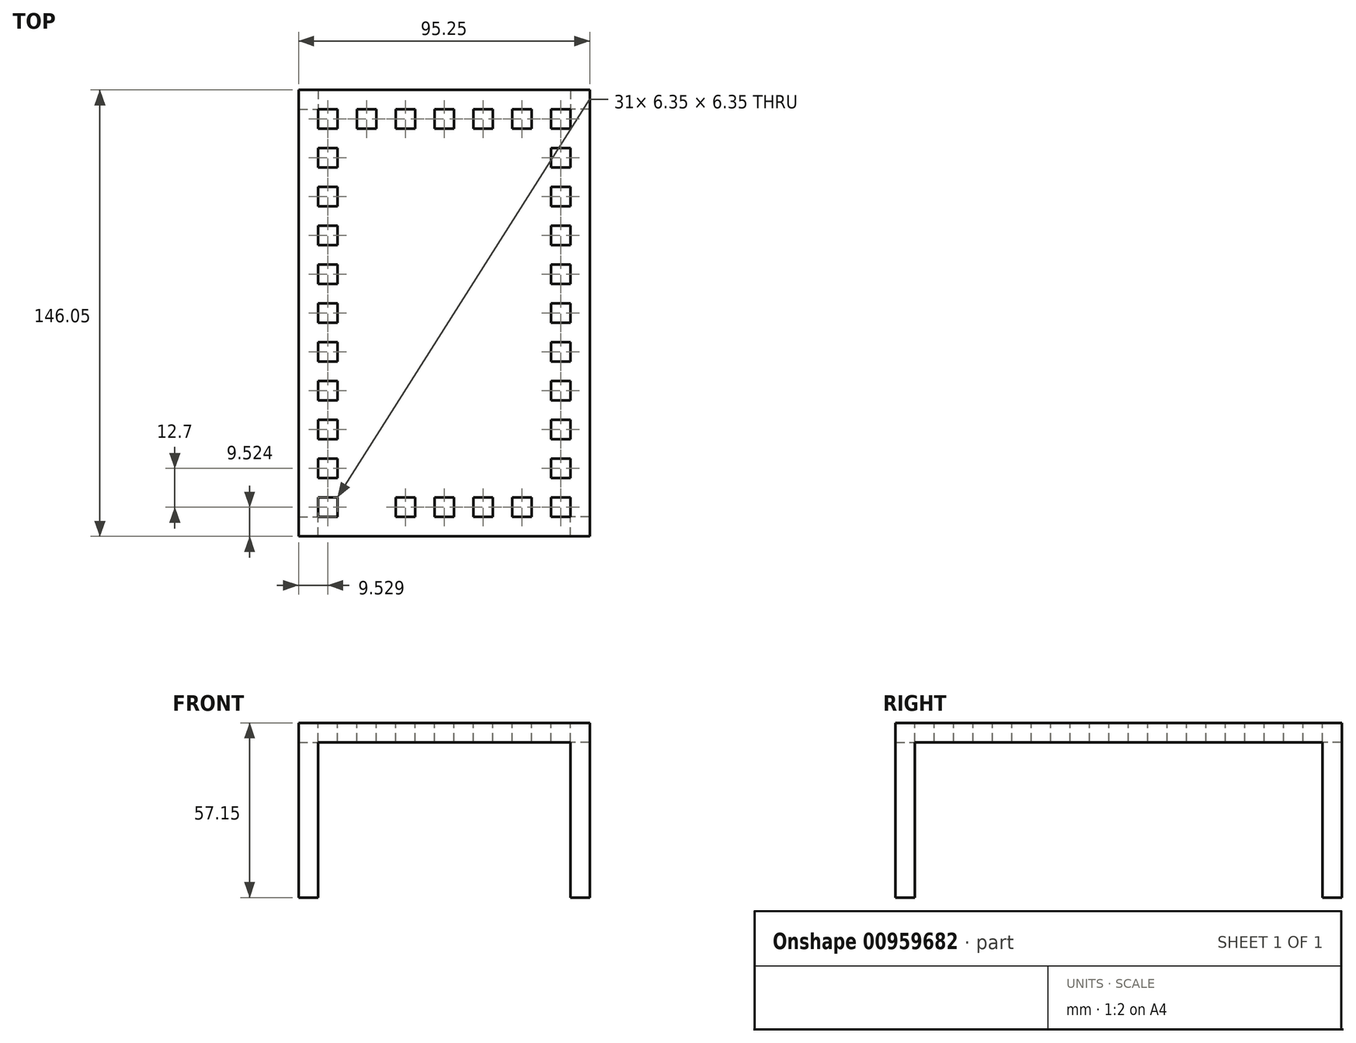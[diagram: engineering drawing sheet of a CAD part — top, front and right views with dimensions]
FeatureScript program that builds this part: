
annotation { "Feature Type Name" : "Feature", "Feature Type Description" : "" }
export const myFeature = defineFeature(function(context is Context, id is Id, definition is map)
    precondition{}
    {
        {
            var Q0;
            Q0=qCreatedBy(makeId("Top.planeOp"),FACE);
            var sketch = newSketch(context, id + "F0", { "sketchPlane" : qUnion([Q0])});
            skLineSegment(sketch, "E0.bottom", {"start": v(-168.58, 47.54) * mm, "end": v(-73.33, 47.54) * mm});
            skLineSegment(sketch, "E0.top", {"start": v(-168.58, -98.51) * mm, "end": v(-73.33, -98.51) * mm});
            skLineSegment(sketch, "E0.left", {"start": v(-168.58, 47.54) * mm, "end": v(-168.58, -98.51) * mm});
            skLineSegment(sketch, "E0.right", {"start": v(-73.33, 47.54) * mm, "end": v(-73.33, -98.51) * mm});
            skSolve(sketch);
        }
        {
            var Q0;
            Q0=makeQuery(id+"F0.imprint","IMPRINT",FACE,{"disambiguationData":[TD([[makeQuery(id+"F0.imprint","IMPRINT",EDGE,{"derivedFrom":sQuery(id+"F0.wireOp",EDGE,"E0.bottom")}),-1.0]])]});
            extrude(context, id + "F1", {"entities" : qUnion([Q0]), "depth" : 6.35 * mm, "offsetDistance" : 25.4 * mm});
        }
        {
            var Q0;
            Q0=makeQuery(id+"F1.opExtrude","CAP_FACE",FACE,{"disambiguationData":[OSD([sQuery(id+"F0.wireOp",EDGE,"E0.bottom"),sQuery(id+"F0.wireOp",EDGE,"E0.top"),sQuery(id+"F0.wireOp",EDGE,"E0.left"),sQuery(id+"F0.wireOp",EDGE,"E0.right")])],"isStart":false});
            var sketch = newSketch(context, id + "F2", { "sketchPlane" : qUnion([Q0])});
            skLineSegment(sketch, "E1.bottom", {"start": v(-162.23, 41.19) * mm, "end": v(-155.88, 41.19) * mm});
            skLineSegment(sketch, "E1.top", {"start": v(-162.23, 34.84) * mm, "end": v(-155.88, 34.84) * mm});
            skLineSegment(sketch, "E1.left", {"start": v(-162.23, 41.19) * mm, "end": v(-162.23, 34.84) * mm});
            skLineSegment(sketch, "E1.right", {"start": v(-155.88, 41.19) * mm, "end": v(-155.88, 34.84) * mm});
            skLineSegment(sketch, "E2.1.0.3", {"start": v(-149.53, 41.19) * mm, "end": v(-149.53, 34.84) * mm});
            skLineSegment(sketch, "E2.2.0.0", {"start": v(-149.53, 41.19) * mm, "end": v(-143.18, 41.19) * mm});
            skLineSegment(sketch, "E2.2.0.1", {"start": v(-149.53, 41.19) * mm, "end": v(-149.53, 34.84) * mm});
            skLineSegment(sketch, "E2.2.0.2", {"start": v(-149.53, 34.84) * mm, "end": v(-143.18, 34.84) * mm});
            skLineSegment(sketch, "E2.2.0.3", {"start": v(-143.18, 41.19) * mm, "end": v(-143.18, 34.84) * mm});
            skLineSegment(sketch, "E2.3.0.1", {"start": v(-143.18, 41.19) * mm, "end": v(-143.18, 34.84) * mm});
            skLineSegment(sketch, "E2.3.0.3", {"start": v(-136.83, 41.19) * mm, "end": v(-136.83, 34.84) * mm});
            skLineSegment(sketch, "E2.4.0.0", {"start": v(-136.83, 41.19) * mm, "end": v(-130.48, 41.19) * mm});
            skLineSegment(sketch, "E2.4.0.1", {"start": v(-136.83, 41.19) * mm, "end": v(-136.83, 34.84) * mm});
            skLineSegment(sketch, "E2.4.0.2", {"start": v(-136.83, 34.84) * mm, "end": v(-130.48, 34.84) * mm});
            skLineSegment(sketch, "E2.4.0.3", {"start": v(-130.48, 41.19) * mm, "end": v(-130.48, 34.84) * mm});
            skLineSegment(sketch, "E2.5.0.1", {"start": v(-130.48, 41.19) * mm, "end": v(-130.48, 34.84) * mm});
            skLineSegment(sketch, "E2.5.0.3", {"start": v(-124.13, 41.19) * mm, "end": v(-124.13, 34.84) * mm});
            skLineSegment(sketch, "E2.6.0.0", {"start": v(-124.13, 41.19) * mm, "end": v(-117.78, 41.19) * mm});
            skLineSegment(sketch, "E2.6.0.1", {"start": v(-124.13, 41.19) * mm, "end": v(-124.13, 34.84) * mm});
            skLineSegment(sketch, "E2.6.0.2", {"start": v(-124.13, 34.84) * mm, "end": v(-117.78, 34.84) * mm});
            skLineSegment(sketch, "E2.6.0.3", {"start": v(-117.78, 41.19) * mm, "end": v(-117.78, 34.84) * mm});
            skLineSegment(sketch, "E2.7.0.1", {"start": v(-117.78, 41.19) * mm, "end": v(-117.78, 34.84) * mm});
            skLineSegment(sketch, "E2.7.0.3", {"start": v(-111.43, 41.19) * mm, "end": v(-111.43, 34.84) * mm});
            skLineSegment(sketch, "E2.8.0.0", {"start": v(-111.43, 41.19) * mm, "end": v(-105.08, 41.19) * mm});
            skLineSegment(sketch, "E2.8.0.1", {"start": v(-111.43, 41.19) * mm, "end": v(-111.43, 34.84) * mm});
            skLineSegment(sketch, "E2.8.0.2", {"start": v(-111.43, 34.84) * mm, "end": v(-105.08, 34.84) * mm});
            skLineSegment(sketch, "E2.8.0.3", {"start": v(-105.08, 41.19) * mm, "end": v(-105.08, 34.84) * mm});
            skLineSegment(sketch, "E2.9.0.1", {"start": v(-105.08, 41.19) * mm, "end": v(-105.08, 34.84) * mm});
            skLineSegment(sketch, "E2.9.0.3", {"start": v(-98.73, 41.19) * mm, "end": v(-98.73, 34.84) * mm});
            skLineSegment(sketch, "E2.10.0.0", {"start": v(-98.73, 41.19) * mm, "end": v(-92.38, 41.19) * mm});
            skLineSegment(sketch, "E2.10.0.1", {"start": v(-98.73, 41.19) * mm, "end": v(-98.73, 34.84) * mm});
            skLineSegment(sketch, "E2.10.0.2", {"start": v(-98.73, 34.84) * mm, "end": v(-92.38, 34.84) * mm});
            skLineSegment(sketch, "E2.10.0.3", {"start": v(-92.38, 41.19) * mm, "end": v(-92.38, 34.84) * mm});
            skLineSegment(sketch, "E2.11.0.1", {"start": v(-92.38, 41.19) * mm, "end": v(-92.38, 34.84) * mm});
            skLineSegment(sketch, "E2.11.0.3", {"start": v(-86.03, 41.19) * mm, "end": v(-86.03, 34.84) * mm});
            skLineSegment(sketch, "E2.12.0.0", {"start": v(-86.03, 41.19) * mm, "end": v(-79.68, 41.19) * mm});
            skLineSegment(sketch, "E2.12.0.1", {"start": v(-86.03, 41.19) * mm, "end": v(-86.03, 34.84) * mm});
            skLineSegment(sketch, "E2.12.0.2", {"start": v(-86.03, 34.84) * mm, "end": v(-79.68, 34.84) * mm});
            skLineSegment(sketch, "E2.12.0.3", {"start": v(-79.68, 41.19) * mm, "end": v(-79.68, 34.84) * mm});
            skLineSegment(sketch, "E2.direction1", {"start": v(-162.23, 41.19) * mm, "end": v(-155.88, 41.19) * mm, "construction": true});
            skLineSegment(sketch, "E3.1.0.3", {"start": v(-124.13, 28.49) * mm, "end": v(-117.78, 28.49) * mm});
            skLineSegment(sketch, "E3.1.0.4", {"start": v(-149.53, 28.49) * mm, "end": v(-143.18, 28.49) * mm});
            skLineSegment(sketch, "E3.1.0.5", {"start": v(-98.73, 28.49) * mm, "end": v(-92.38, 28.49) * mm});
            skLineSegment(sketch, "E3.1.0.17", {"start": v(-162.23, 28.49) * mm, "end": v(-155.88, 28.49) * mm});
            skLineSegment(sketch, "E3.1.0.30", {"start": v(-86.03, 28.49) * mm, "end": v(-79.68, 28.49) * mm});
            skLineSegment(sketch, "E3.1.0.31", {"start": v(-111.43, 28.49) * mm, "end": v(-105.08, 28.49) * mm});
            skLineSegment(sketch, "E3.1.0.32", {"start": v(-136.83, 28.49) * mm, "end": v(-130.48, 28.49) * mm});
            skLineSegment(sketch, "E3.2.0.0", {"start": v(-149.53, 28.49) * mm, "end": v(-143.18, 28.49) * mm});
            skLineSegment(sketch, "E3.2.0.1", {"start": v(-149.53, 28.49) * mm, "end": v(-149.53, 22.14) * mm});
            skLineSegment(sketch, "E3.2.0.3", {"start": v(-124.13, 22.14) * mm, "end": v(-117.78, 22.14) * mm});
            skLineSegment(sketch, "E3.2.0.4", {"start": v(-149.53, 22.14) * mm, "end": v(-143.18, 22.14) * mm});
            skLineSegment(sketch, "E3.2.0.5", {"start": v(-98.73, 22.14) * mm, "end": v(-92.38, 22.14) * mm});
            skLineSegment(sketch, "E3.2.0.7", {"start": v(-98.73, 28.49) * mm, "end": v(-92.38, 28.49) * mm});
            skLineSegment(sketch, "E3.2.0.8", {"start": v(-124.13, 28.49) * mm, "end": v(-117.78, 28.49) * mm});
            skLineSegment(sketch, "E3.2.0.11", {"start": v(-143.18, 28.49) * mm, "end": v(-143.18, 22.14) * mm});
            skLineSegment(sketch, "E3.2.0.12", {"start": v(-98.73, 28.49) * mm, "end": v(-98.73, 22.14) * mm});
            skLineSegment(sketch, "E3.2.0.13", {"start": v(-124.13, 28.49) * mm, "end": v(-124.13, 22.14) * mm});
            skLineSegment(sketch, "E3.2.0.17", {"start": v(-162.23, 22.14) * mm, "end": v(-155.88, 22.14) * mm});
            skLineSegment(sketch, "E3.2.0.20", {"start": v(-162.23, 28.49) * mm, "end": v(-162.23, 22.14) * mm});
            skLineSegment(sketch, "E3.2.0.21", {"start": v(-162.23, 28.49) * mm, "end": v(-155.88, 28.49) * mm, "construction": true});
            skLineSegment(sketch, "E3.2.0.22", {"start": v(-92.38, 28.49) * mm, "end": v(-92.38, 22.14) * mm});
            skLineSegment(sketch, "E3.2.0.24", {"start": v(-117.78, 28.49) * mm, "end": v(-117.78, 22.14) * mm});
            skLineSegment(sketch, "E3.2.0.26", {"start": v(-79.68, 28.49) * mm, "end": v(-79.68, 22.14) * mm});
            skLineSegment(sketch, "E3.2.0.27", {"start": v(-105.08, 28.49) * mm, "end": v(-105.08, 22.14) * mm});
            skLineSegment(sketch, "E3.2.0.28", {"start": v(-130.48, 28.49) * mm, "end": v(-130.48, 22.14) * mm});
            skLineSegment(sketch, "E3.2.0.30", {"start": v(-86.03, 22.14) * mm, "end": v(-79.68, 22.14) * mm});
            skLineSegment(sketch, "E3.2.0.31", {"start": v(-111.43, 22.14) * mm, "end": v(-105.08, 22.14) * mm});
            skLineSegment(sketch, "E3.2.0.32", {"start": v(-136.83, 22.14) * mm, "end": v(-130.48, 22.14) * mm});
            skLineSegment(sketch, "E3.2.0.33", {"start": v(-155.88, 28.49) * mm, "end": v(-155.88, 22.14) * mm});
            skLineSegment(sketch, "E3.2.0.34", {"start": v(-86.03, 28.49) * mm, "end": v(-86.03, 22.14) * mm});
            skLineSegment(sketch, "E3.2.0.35", {"start": v(-111.43, 28.49) * mm, "end": v(-111.43, 22.14) * mm});
            skLineSegment(sketch, "E3.2.0.36", {"start": v(-136.83, 28.49) * mm, "end": v(-136.83, 22.14) * mm});
            skLineSegment(sketch, "E3.2.0.37", {"start": v(-86.03, 28.49) * mm, "end": v(-79.68, 28.49) * mm});
            skLineSegment(sketch, "E3.2.0.38", {"start": v(-111.43, 28.49) * mm, "end": v(-105.08, 28.49) * mm});
            skLineSegment(sketch, "E3.2.0.39", {"start": v(-136.83, 28.49) * mm, "end": v(-130.48, 28.49) * mm});
            skLineSegment(sketch, "E3.2.0.40", {"start": v(-98.73, 28.49) * mm, "end": v(-98.73, 22.14) * mm});
            skLineSegment(sketch, "E3.2.0.41", {"start": v(-117.78, 28.49) * mm, "end": v(-117.78, 22.14) * mm});
            skLineSegment(sketch, "E3.2.0.42", {"start": v(-136.83, 28.49) * mm, "end": v(-136.83, 22.14) * mm});
            skLineSegment(sketch, "E3.2.0.43", {"start": v(-143.18, 28.49) * mm, "end": v(-143.18, 22.14) * mm});
            skLineSegment(sketch, "E3.2.0.44", {"start": v(-124.13, 28.49) * mm, "end": v(-124.13, 22.14) * mm});
            skLineSegment(sketch, "E3.2.0.45", {"start": v(-149.53, 28.49) * mm, "end": v(-149.53, 22.14) * mm});
            skLineSegment(sketch, "E3.2.0.46", {"start": v(-92.38, 28.49) * mm, "end": v(-92.38, 22.14) * mm});
            skLineSegment(sketch, "E3.2.0.47", {"start": v(-162.23, 28.49) * mm, "end": v(-155.88, 28.49) * mm});
            skLineSegment(sketch, "E3.2.0.48", {"start": v(-105.08, 28.49) * mm, "end": v(-105.08, 22.14) * mm});
            skLineSegment(sketch, "E3.2.0.49", {"start": v(-130.48, 28.49) * mm, "end": v(-130.48, 22.14) * mm});
            skLineSegment(sketch, "E3.2.0.50", {"start": v(-155.88, 28.49) * mm, "end": v(-155.88, 22.14) * mm});
            skLineSegment(sketch, "E3.2.0.51", {"start": v(-86.03, 28.49) * mm, "end": v(-86.03, 22.14) * mm});
            skLineSegment(sketch, "E3.2.0.52", {"start": v(-111.43, 28.49) * mm, "end": v(-111.43, 22.14) * mm});
            skLineSegment(sketch, "E3.3.0.0", {"start": v(-149.53, 22.14) * mm, "end": v(-143.18, 22.14) * mm});
            skLineSegment(sketch, "E3.3.0.3", {"start": v(-124.13, 15.79) * mm, "end": v(-117.78, 15.79) * mm});
            skLineSegment(sketch, "E3.3.0.4", {"start": v(-149.53, 15.79) * mm, "end": v(-143.18, 15.79) * mm});
            skLineSegment(sketch, "E3.3.0.5", {"start": v(-98.73, 15.79) * mm, "end": v(-92.38, 15.79) * mm});
            skLineSegment(sketch, "E3.3.0.7", {"start": v(-98.73, 22.14) * mm, "end": v(-92.38, 22.14) * mm});
            skLineSegment(sketch, "E3.3.0.8", {"start": v(-124.13, 22.14) * mm, "end": v(-117.78, 22.14) * mm});
            skLineSegment(sketch, "E3.3.0.17", {"start": v(-162.23, 15.79) * mm, "end": v(-155.88, 15.79) * mm});
            skLineSegment(sketch, "E3.3.0.21", {"start": v(-162.23, 22.14) * mm, "end": v(-155.88, 22.14) * mm, "construction": true});
            skLineSegment(sketch, "E3.3.0.30", {"start": v(-86.03, 15.79) * mm, "end": v(-79.68, 15.79) * mm});
            skLineSegment(sketch, "E3.3.0.31", {"start": v(-111.43, 15.79) * mm, "end": v(-105.08, 15.79) * mm});
            skLineSegment(sketch, "E3.3.0.32", {"start": v(-136.83, 15.79) * mm, "end": v(-130.48, 15.79) * mm});
            skLineSegment(sketch, "E3.3.0.37", {"start": v(-86.03, 22.14) * mm, "end": v(-79.68, 22.14) * mm});
            skLineSegment(sketch, "E3.3.0.38", {"start": v(-111.43, 22.14) * mm, "end": v(-105.08, 22.14) * mm});
            skLineSegment(sketch, "E3.3.0.39", {"start": v(-136.83, 22.14) * mm, "end": v(-130.48, 22.14) * mm});
            skLineSegment(sketch, "E3.3.0.47", {"start": v(-162.23, 22.14) * mm, "end": v(-155.88, 22.14) * mm});
            skLineSegment(sketch, "E3.4.0.0", {"start": v(-149.53, 15.79) * mm, "end": v(-143.18, 15.79) * mm});
            skLineSegment(sketch, "E3.4.0.1", {"start": v(-149.53, 15.79) * mm, "end": v(-149.53, 9.44) * mm});
            skLineSegment(sketch, "E3.4.0.3", {"start": v(-124.13, 9.44) * mm, "end": v(-117.78, 9.44) * mm});
            skLineSegment(sketch, "E3.4.0.4", {"start": v(-149.53, 9.44) * mm, "end": v(-143.18, 9.44) * mm});
            skLineSegment(sketch, "E3.4.0.5", {"start": v(-98.73, 9.44) * mm, "end": v(-92.38, 9.44) * mm});
            skLineSegment(sketch, "E3.4.0.7", {"start": v(-98.73, 15.79) * mm, "end": v(-92.38, 15.79) * mm});
            skLineSegment(sketch, "E3.4.0.8", {"start": v(-124.13, 15.79) * mm, "end": v(-117.78, 15.79) * mm});
            skLineSegment(sketch, "E3.4.0.11", {"start": v(-143.18, 15.79) * mm, "end": v(-143.18, 9.44) * mm});
            skLineSegment(sketch, "E3.4.0.12", {"start": v(-98.73, 15.79) * mm, "end": v(-98.73, 9.44) * mm});
            skLineSegment(sketch, "E3.4.0.13", {"start": v(-124.13, 15.79) * mm, "end": v(-124.13, 9.44) * mm});
            skLineSegment(sketch, "E3.4.0.17", {"start": v(-162.23, 9.44) * mm, "end": v(-155.88, 9.44) * mm});
            skLineSegment(sketch, "E3.4.0.20", {"start": v(-162.23, 15.79) * mm, "end": v(-162.23, 9.44) * mm});
            skLineSegment(sketch, "E3.4.0.21", {"start": v(-162.23, 15.79) * mm, "end": v(-155.88, 15.79) * mm, "construction": true});
            skLineSegment(sketch, "E3.4.0.22", {"start": v(-92.38, 15.79) * mm, "end": v(-92.38, 9.44) * mm});
            skLineSegment(sketch, "E3.4.0.24", {"start": v(-117.78, 15.79) * mm, "end": v(-117.78, 9.44) * mm});
            skLineSegment(sketch, "E3.4.0.26", {"start": v(-79.68, 15.79) * mm, "end": v(-79.68, 9.44) * mm});
            skLineSegment(sketch, "E3.4.0.27", {"start": v(-105.08, 15.79) * mm, "end": v(-105.08, 9.44) * mm});
            skLineSegment(sketch, "E3.4.0.28", {"start": v(-130.48, 15.79) * mm, "end": v(-130.48, 9.44) * mm});
            skLineSegment(sketch, "E3.4.0.30", {"start": v(-86.03, 9.44) * mm, "end": v(-79.68, 9.44) * mm});
            skLineSegment(sketch, "E3.4.0.31", {"start": v(-111.43, 9.44) * mm, "end": v(-105.08, 9.44) * mm});
            skLineSegment(sketch, "E3.4.0.32", {"start": v(-136.83, 9.44) * mm, "end": v(-130.48, 9.44) * mm});
            skLineSegment(sketch, "E3.4.0.33", {"start": v(-155.88, 15.79) * mm, "end": v(-155.88, 9.44) * mm});
            skLineSegment(sketch, "E3.4.0.34", {"start": v(-86.03, 15.79) * mm, "end": v(-86.03, 9.44) * mm});
            skLineSegment(sketch, "E3.4.0.35", {"start": v(-111.43, 15.79) * mm, "end": v(-111.43, 9.44) * mm});
            skLineSegment(sketch, "E3.4.0.36", {"start": v(-136.83, 15.79) * mm, "end": v(-136.83, 9.44) * mm});
            skLineSegment(sketch, "E3.4.0.37", {"start": v(-86.03, 15.79) * mm, "end": v(-79.68, 15.79) * mm});
            skLineSegment(sketch, "E3.4.0.38", {"start": v(-111.43, 15.79) * mm, "end": v(-105.08, 15.79) * mm});
            skLineSegment(sketch, "E3.4.0.39", {"start": v(-136.83, 15.79) * mm, "end": v(-130.48, 15.79) * mm});
            skLineSegment(sketch, "E3.4.0.40", {"start": v(-98.73, 15.79) * mm, "end": v(-98.73, 9.44) * mm});
            skLineSegment(sketch, "E3.4.0.41", {"start": v(-117.78, 15.79) * mm, "end": v(-117.78, 9.44) * mm});
            skLineSegment(sketch, "E3.4.0.42", {"start": v(-136.83, 15.79) * mm, "end": v(-136.83, 9.44) * mm});
            skLineSegment(sketch, "E3.4.0.43", {"start": v(-143.18, 15.79) * mm, "end": v(-143.18, 9.44) * mm});
            skLineSegment(sketch, "E3.4.0.44", {"start": v(-124.13, 15.79) * mm, "end": v(-124.13, 9.44) * mm});
            skLineSegment(sketch, "E3.4.0.45", {"start": v(-149.53, 15.79) * mm, "end": v(-149.53, 9.44) * mm});
            skLineSegment(sketch, "E3.4.0.46", {"start": v(-92.38, 15.79) * mm, "end": v(-92.38, 9.44) * mm});
            skLineSegment(sketch, "E3.4.0.47", {"start": v(-162.23, 15.79) * mm, "end": v(-155.88, 15.79) * mm});
            skLineSegment(sketch, "E3.4.0.48", {"start": v(-105.08, 15.79) * mm, "end": v(-105.08, 9.44) * mm});
            skLineSegment(sketch, "E3.4.0.49", {"start": v(-130.48, 15.79) * mm, "end": v(-130.48, 9.44) * mm});
            skLineSegment(sketch, "E3.4.0.50", {"start": v(-155.88, 15.79) * mm, "end": v(-155.88, 9.44) * mm});
            skLineSegment(sketch, "E3.4.0.51", {"start": v(-86.03, 15.79) * mm, "end": v(-86.03, 9.44) * mm});
            skLineSegment(sketch, "E3.4.0.52", {"start": v(-111.43, 15.79) * mm, "end": v(-111.43, 9.44) * mm});
            skLineSegment(sketch, "E3.5.0.0", {"start": v(-149.53, 9.44) * mm, "end": v(-143.18, 9.44) * mm});
            skLineSegment(sketch, "E3.5.0.3", {"start": v(-124.13, 3.09) * mm, "end": v(-117.78, 3.09) * mm});
            skLineSegment(sketch, "E3.5.0.4", {"start": v(-149.53, 3.09) * mm, "end": v(-143.18, 3.09) * mm});
            skLineSegment(sketch, "E3.5.0.5", {"start": v(-98.73, 3.09) * mm, "end": v(-92.38, 3.09) * mm});
            skLineSegment(sketch, "E3.5.0.7", {"start": v(-98.73, 9.44) * mm, "end": v(-92.38, 9.44) * mm});
            skLineSegment(sketch, "E3.5.0.8", {"start": v(-124.13, 9.44) * mm, "end": v(-117.78, 9.44) * mm});
            skLineSegment(sketch, "E3.5.0.17", {"start": v(-162.23, 3.09) * mm, "end": v(-155.88, 3.09) * mm});
            skLineSegment(sketch, "E3.5.0.21", {"start": v(-162.23, 9.44) * mm, "end": v(-155.88, 9.44) * mm, "construction": true});
            skLineSegment(sketch, "E3.5.0.30", {"start": v(-86.03, 3.09) * mm, "end": v(-79.68, 3.09) * mm});
            skLineSegment(sketch, "E3.5.0.31", {"start": v(-111.43, 3.09) * mm, "end": v(-105.08, 3.09) * mm});
            skLineSegment(sketch, "E3.5.0.32", {"start": v(-136.83, 3.09) * mm, "end": v(-130.48, 3.09) * mm});
            skLineSegment(sketch, "E3.5.0.37", {"start": v(-86.03, 9.44) * mm, "end": v(-79.68, 9.44) * mm});
            skLineSegment(sketch, "E3.5.0.38", {"start": v(-111.43, 9.44) * mm, "end": v(-105.08, 9.44) * mm});
            skLineSegment(sketch, "E3.5.0.39", {"start": v(-136.83, 9.44) * mm, "end": v(-130.48, 9.44) * mm});
            skLineSegment(sketch, "E3.5.0.47", {"start": v(-162.23, 9.44) * mm, "end": v(-155.88, 9.44) * mm});
            skLineSegment(sketch, "E3.6.0.0", {"start": v(-149.53, 3.09) * mm, "end": v(-143.18, 3.09) * mm});
            skLineSegment(sketch, "E3.6.0.1", {"start": v(-149.53, 3.09) * mm, "end": v(-149.53, -3.26) * mm});
            skLineSegment(sketch, "E3.6.0.3", {"start": v(-124.13, -3.26) * mm, "end": v(-117.78, -3.26) * mm});
            skLineSegment(sketch, "E3.6.0.4", {"start": v(-149.53, -3.26) * mm, "end": v(-143.18, -3.26) * mm});
            skLineSegment(sketch, "E3.6.0.5", {"start": v(-98.73, -3.26) * mm, "end": v(-92.38, -3.26) * mm});
            skLineSegment(sketch, "E3.6.0.7", {"start": v(-98.73, 3.09) * mm, "end": v(-92.38, 3.09) * mm});
            skLineSegment(sketch, "E3.6.0.8", {"start": v(-124.13, 3.09) * mm, "end": v(-117.78, 3.09) * mm});
            skLineSegment(sketch, "E3.6.0.11", {"start": v(-143.18, 3.09) * mm, "end": v(-143.18, -3.26) * mm});
            skLineSegment(sketch, "E3.6.0.12", {"start": v(-98.73, 3.09) * mm, "end": v(-98.73, -3.26) * mm});
            skLineSegment(sketch, "E3.6.0.13", {"start": v(-124.13, 3.09) * mm, "end": v(-124.13, -3.26) * mm});
            skLineSegment(sketch, "E3.6.0.17", {"start": v(-162.23, -3.26) * mm, "end": v(-155.88, -3.26) * mm});
            skLineSegment(sketch, "E3.6.0.20", {"start": v(-162.23, 3.09) * mm, "end": v(-162.23, -3.26) * mm});
            skLineSegment(sketch, "E3.6.0.21", {"start": v(-162.23, 3.09) * mm, "end": v(-155.88, 3.09) * mm, "construction": true});
            skLineSegment(sketch, "E3.6.0.22", {"start": v(-92.38, 3.09) * mm, "end": v(-92.38, -3.26) * mm});
            skLineSegment(sketch, "E3.6.0.24", {"start": v(-117.78, 3.09) * mm, "end": v(-117.78, -3.26) * mm});
            skLineSegment(sketch, "E3.6.0.26", {"start": v(-79.68, 3.09) * mm, "end": v(-79.68, -3.26) * mm});
            skLineSegment(sketch, "E3.6.0.27", {"start": v(-105.08, 3.09) * mm, "end": v(-105.08, -3.26) * mm});
            skLineSegment(sketch, "E3.6.0.28", {"start": v(-130.48, 3.09) * mm, "end": v(-130.48, -3.26) * mm});
            skLineSegment(sketch, "E3.6.0.30", {"start": v(-86.03, -3.26) * mm, "end": v(-79.68, -3.26) * mm});
            skLineSegment(sketch, "E3.6.0.31", {"start": v(-111.43, -3.26) * mm, "end": v(-105.08, -3.26) * mm});
            skLineSegment(sketch, "E3.6.0.32", {"start": v(-136.83, -3.26) * mm, "end": v(-130.48, -3.26) * mm});
            skLineSegment(sketch, "E3.6.0.33", {"start": v(-155.88, 3.09) * mm, "end": v(-155.88, -3.26) * mm});
            skLineSegment(sketch, "E3.6.0.34", {"start": v(-86.03, 3.09) * mm, "end": v(-86.03, -3.26) * mm});
            skLineSegment(sketch, "E3.6.0.35", {"start": v(-111.43, 3.09) * mm, "end": v(-111.43, -3.26) * mm});
            skLineSegment(sketch, "E3.6.0.36", {"start": v(-136.83, 3.09) * mm, "end": v(-136.83, -3.26) * mm});
            skLineSegment(sketch, "E3.6.0.37", {"start": v(-86.03, 3.09) * mm, "end": v(-79.68, 3.09) * mm});
            skLineSegment(sketch, "E3.6.0.38", {"start": v(-111.43, 3.09) * mm, "end": v(-105.08, 3.09) * mm});
            skLineSegment(sketch, "E3.6.0.39", {"start": v(-136.83, 3.09) * mm, "end": v(-130.48, 3.09) * mm});
            skLineSegment(sketch, "E3.6.0.40", {"start": v(-98.73, 3.09) * mm, "end": v(-98.73, -3.26) * mm});
            skLineSegment(sketch, "E3.6.0.41", {"start": v(-117.78, 3.09) * mm, "end": v(-117.78, -3.26) * mm});
            skLineSegment(sketch, "E3.6.0.42", {"start": v(-136.83, 3.09) * mm, "end": v(-136.83, -3.26) * mm});
            skLineSegment(sketch, "E3.6.0.43", {"start": v(-143.18, 3.09) * mm, "end": v(-143.18, -3.26) * mm});
            skLineSegment(sketch, "E3.6.0.44", {"start": v(-124.13, 3.09) * mm, "end": v(-124.13, -3.26) * mm});
            skLineSegment(sketch, "E3.6.0.45", {"start": v(-149.53, 3.09) * mm, "end": v(-149.53, -3.26) * mm});
            skLineSegment(sketch, "E3.6.0.46", {"start": v(-92.38, 3.09) * mm, "end": v(-92.38, -3.26) * mm});
            skLineSegment(sketch, "E3.6.0.47", {"start": v(-162.23, 3.09) * mm, "end": v(-155.88, 3.09) * mm});
            skLineSegment(sketch, "E3.6.0.48", {"start": v(-105.08, 3.09) * mm, "end": v(-105.08, -3.26) * mm});
            skLineSegment(sketch, "E3.6.0.49", {"start": v(-130.48, 3.09) * mm, "end": v(-130.48, -3.26) * mm});
            skLineSegment(sketch, "E3.6.0.50", {"start": v(-155.88, 3.09) * mm, "end": v(-155.88, -3.26) * mm});
            skLineSegment(sketch, "E3.6.0.51", {"start": v(-86.03, 3.09) * mm, "end": v(-86.03, -3.26) * mm});
            skLineSegment(sketch, "E3.6.0.52", {"start": v(-111.43, 3.09) * mm, "end": v(-111.43, -3.26) * mm});
            skLineSegment(sketch, "E3.7.0.0", {"start": v(-149.53, -3.26) * mm, "end": v(-143.18, -3.26) * mm});
            skLineSegment(sketch, "E3.7.0.3", {"start": v(-124.13, -9.61) * mm, "end": v(-117.78, -9.61) * mm});
            skLineSegment(sketch, "E3.7.0.4", {"start": v(-149.53, -9.61) * mm, "end": v(-143.18, -9.61) * mm});
            skLineSegment(sketch, "E3.7.0.5", {"start": v(-98.73, -9.61) * mm, "end": v(-92.38, -9.61) * mm});
            skLineSegment(sketch, "E3.7.0.7", {"start": v(-98.73, -3.26) * mm, "end": v(-92.38, -3.26) * mm});
            skLineSegment(sketch, "E3.7.0.8", {"start": v(-124.13, -3.26) * mm, "end": v(-117.78, -3.26) * mm});
            skLineSegment(sketch, "E3.7.0.17", {"start": v(-162.23, -9.61) * mm, "end": v(-155.88, -9.61) * mm});
            skLineSegment(sketch, "E3.7.0.21", {"start": v(-162.23, -3.26) * mm, "end": v(-155.88, -3.26) * mm, "construction": true});
            skLineSegment(sketch, "E3.7.0.30", {"start": v(-86.03, -9.61) * mm, "end": v(-79.68, -9.61) * mm});
            skLineSegment(sketch, "E3.7.0.31", {"start": v(-111.43, -9.61) * mm, "end": v(-105.08, -9.61) * mm});
            skLineSegment(sketch, "E3.7.0.32", {"start": v(-136.83, -9.61) * mm, "end": v(-130.48, -9.61) * mm});
            skLineSegment(sketch, "E3.7.0.37", {"start": v(-86.03, -3.26) * mm, "end": v(-79.68, -3.26) * mm});
            skLineSegment(sketch, "E3.7.0.38", {"start": v(-111.43, -3.26) * mm, "end": v(-105.08, -3.26) * mm});
            skLineSegment(sketch, "E3.7.0.39", {"start": v(-136.83, -3.26) * mm, "end": v(-130.48, -3.26) * mm});
            skLineSegment(sketch, "E3.7.0.47", {"start": v(-162.23, -3.26) * mm, "end": v(-155.88, -3.26) * mm});
            skLineSegment(sketch, "E3.8.0.0", {"start": v(-149.53, -9.61) * mm, "end": v(-143.18, -9.61) * mm});
            skLineSegment(sketch, "E3.8.0.1", {"start": v(-149.53, -9.61) * mm, "end": v(-149.53, -15.96) * mm});
            skLineSegment(sketch, "E3.8.0.3", {"start": v(-124.13, -15.96) * mm, "end": v(-117.78, -15.96) * mm});
            skLineSegment(sketch, "E3.8.0.4", {"start": v(-149.53, -15.96) * mm, "end": v(-143.18, -15.96) * mm});
            skLineSegment(sketch, "E3.8.0.5", {"start": v(-98.73, -15.96) * mm, "end": v(-92.38, -15.96) * mm});
            skLineSegment(sketch, "E3.8.0.7", {"start": v(-98.73, -9.61) * mm, "end": v(-92.38, -9.61) * mm});
            skLineSegment(sketch, "E3.8.0.8", {"start": v(-124.13, -9.61) * mm, "end": v(-117.78, -9.61) * mm});
            skLineSegment(sketch, "E3.8.0.11", {"start": v(-143.18, -9.61) * mm, "end": v(-143.18, -15.96) * mm});
            skLineSegment(sketch, "E3.8.0.12", {"start": v(-98.73, -9.61) * mm, "end": v(-98.73, -15.96) * mm});
            skLineSegment(sketch, "E3.8.0.13", {"start": v(-124.13, -9.61) * mm, "end": v(-124.13, -15.96) * mm});
            skLineSegment(sketch, "E3.8.0.17", {"start": v(-162.23, -15.96) * mm, "end": v(-155.88, -15.96) * mm});
            skLineSegment(sketch, "E3.8.0.20", {"start": v(-162.23, -9.61) * mm, "end": v(-162.23, -15.96) * mm});
            skLineSegment(sketch, "E3.8.0.21", {"start": v(-162.23, -9.61) * mm, "end": v(-155.88, -9.61) * mm, "construction": true});
            skLineSegment(sketch, "E3.8.0.22", {"start": v(-92.38, -9.61) * mm, "end": v(-92.38, -15.96) * mm});
            skLineSegment(sketch, "E3.8.0.24", {"start": v(-117.78, -9.61) * mm, "end": v(-117.78, -15.96) * mm});
            skLineSegment(sketch, "E3.8.0.26", {"start": v(-79.68, -9.61) * mm, "end": v(-79.68, -15.96) * mm});
            skLineSegment(sketch, "E3.8.0.27", {"start": v(-105.08, -9.61) * mm, "end": v(-105.08, -15.96) * mm});
            skLineSegment(sketch, "E3.8.0.28", {"start": v(-130.48, -9.61) * mm, "end": v(-130.48, -15.96) * mm});
            skLineSegment(sketch, "E3.8.0.30", {"start": v(-86.03, -15.96) * mm, "end": v(-79.68, -15.96) * mm});
            skLineSegment(sketch, "E3.8.0.31", {"start": v(-111.43, -15.96) * mm, "end": v(-105.08, -15.96) * mm});
            skLineSegment(sketch, "E3.8.0.32", {"start": v(-136.83, -15.96) * mm, "end": v(-130.48, -15.96) * mm});
            skLineSegment(sketch, "E3.8.0.33", {"start": v(-155.88, -9.61) * mm, "end": v(-155.88, -15.96) * mm});
            skLineSegment(sketch, "E3.8.0.34", {"start": v(-86.03, -9.61) * mm, "end": v(-86.03, -15.96) * mm});
            skLineSegment(sketch, "E3.8.0.35", {"start": v(-111.43, -9.61) * mm, "end": v(-111.43, -15.96) * mm});
            skLineSegment(sketch, "E3.8.0.36", {"start": v(-136.83, -9.61) * mm, "end": v(-136.83, -15.96) * mm});
            skLineSegment(sketch, "E3.8.0.37", {"start": v(-86.03, -9.61) * mm, "end": v(-79.68, -9.61) * mm});
            skLineSegment(sketch, "E3.8.0.38", {"start": v(-111.43, -9.61) * mm, "end": v(-105.08, -9.61) * mm});
            skLineSegment(sketch, "E3.8.0.39", {"start": v(-136.83, -9.61) * mm, "end": v(-130.48, -9.61) * mm});
            skLineSegment(sketch, "E3.8.0.40", {"start": v(-98.73, -9.61) * mm, "end": v(-98.73, -15.96) * mm});
            skLineSegment(sketch, "E3.8.0.41", {"start": v(-117.78, -9.61) * mm, "end": v(-117.78, -15.96) * mm});
            skLineSegment(sketch, "E3.8.0.42", {"start": v(-136.83, -9.61) * mm, "end": v(-136.83, -15.96) * mm});
            skLineSegment(sketch, "E3.8.0.43", {"start": v(-143.18, -9.61) * mm, "end": v(-143.18, -15.96) * mm});
            skLineSegment(sketch, "E3.8.0.44", {"start": v(-124.13, -9.61) * mm, "end": v(-124.13, -15.96) * mm});
            skLineSegment(sketch, "E3.8.0.45", {"start": v(-149.53, -9.61) * mm, "end": v(-149.53, -15.96) * mm});
            skLineSegment(sketch, "E3.8.0.46", {"start": v(-92.38, -9.61) * mm, "end": v(-92.38, -15.96) * mm});
            skLineSegment(sketch, "E3.8.0.47", {"start": v(-162.23, -9.61) * mm, "end": v(-155.88, -9.61) * mm});
            skLineSegment(sketch, "E3.8.0.48", {"start": v(-105.08, -9.61) * mm, "end": v(-105.08, -15.96) * mm});
            skLineSegment(sketch, "E3.8.0.49", {"start": v(-130.48, -9.61) * mm, "end": v(-130.48, -15.96) * mm});
            skLineSegment(sketch, "E3.8.0.50", {"start": v(-155.88, -9.61) * mm, "end": v(-155.88, -15.96) * mm});
            skLineSegment(sketch, "E3.8.0.51", {"start": v(-86.03, -9.61) * mm, "end": v(-86.03, -15.96) * mm});
            skLineSegment(sketch, "E3.8.0.52", {"start": v(-111.43, -9.61) * mm, "end": v(-111.43, -15.96) * mm});
            skLineSegment(sketch, "E3.9.0.0", {"start": v(-149.53, -15.96) * mm, "end": v(-143.18, -15.96) * mm});
            skLineSegment(sketch, "E3.9.0.3", {"start": v(-124.13, -22.31) * mm, "end": v(-117.78, -22.31) * mm});
            skLineSegment(sketch, "E3.9.0.4", {"start": v(-149.53, -22.31) * mm, "end": v(-143.18, -22.31) * mm});
            skLineSegment(sketch, "E3.9.0.5", {"start": v(-98.73, -22.31) * mm, "end": v(-92.38, -22.31) * mm});
            skLineSegment(sketch, "E3.9.0.7", {"start": v(-98.73, -15.96) * mm, "end": v(-92.38, -15.96) * mm});
            skLineSegment(sketch, "E3.9.0.8", {"start": v(-124.13, -15.96) * mm, "end": v(-117.78, -15.96) * mm});
            skLineSegment(sketch, "E3.9.0.17", {"start": v(-162.23, -22.31) * mm, "end": v(-155.88, -22.31) * mm});
            skLineSegment(sketch, "E3.9.0.21", {"start": v(-162.23, -15.96) * mm, "end": v(-155.88, -15.96) * mm, "construction": true});
            skLineSegment(sketch, "E3.9.0.30", {"start": v(-86.03, -22.31) * mm, "end": v(-79.68, -22.31) * mm});
            skLineSegment(sketch, "E3.9.0.31", {"start": v(-111.43, -22.31) * mm, "end": v(-105.08, -22.31) * mm});
            skLineSegment(sketch, "E3.9.0.32", {"start": v(-136.83, -22.31) * mm, "end": v(-130.48, -22.31) * mm});
            skLineSegment(sketch, "E3.9.0.37", {"start": v(-86.03, -15.96) * mm, "end": v(-79.68, -15.96) * mm});
            skLineSegment(sketch, "E3.9.0.38", {"start": v(-111.43, -15.96) * mm, "end": v(-105.08, -15.96) * mm});
            skLineSegment(sketch, "E3.9.0.39", {"start": v(-136.83, -15.96) * mm, "end": v(-130.48, -15.96) * mm});
            skLineSegment(sketch, "E3.9.0.47", {"start": v(-162.23, -15.96) * mm, "end": v(-155.88, -15.96) * mm});
            skLineSegment(sketch, "E3.10.0.0", {"start": v(-149.53, -22.31) * mm, "end": v(-143.18, -22.31) * mm});
            skLineSegment(sketch, "E3.10.0.1", {"start": v(-149.53, -22.31) * mm, "end": v(-149.53, -28.66) * mm});
            skLineSegment(sketch, "E3.10.0.3", {"start": v(-124.13, -28.66) * mm, "end": v(-117.78, -28.66) * mm});
            skLineSegment(sketch, "E3.10.0.4", {"start": v(-149.53, -28.66) * mm, "end": v(-143.18, -28.66) * mm});
            skLineSegment(sketch, "E3.10.0.5", {"start": v(-98.73, -28.66) * mm, "end": v(-92.38, -28.66) * mm});
            skLineSegment(sketch, "E3.10.0.7", {"start": v(-98.73, -22.31) * mm, "end": v(-92.38, -22.31) * mm});
            skLineSegment(sketch, "E3.10.0.8", {"start": v(-124.13, -22.31) * mm, "end": v(-117.78, -22.31) * mm});
            skLineSegment(sketch, "E3.10.0.11", {"start": v(-143.18, -22.31) * mm, "end": v(-143.18, -28.66) * mm});
            skLineSegment(sketch, "E3.10.0.12", {"start": v(-98.73, -22.31) * mm, "end": v(-98.73, -28.66) * mm});
            skLineSegment(sketch, "E3.10.0.13", {"start": v(-124.13, -22.31) * mm, "end": v(-124.13, -28.66) * mm});
            skLineSegment(sketch, "E3.10.0.17", {"start": v(-162.23, -28.66) * mm, "end": v(-155.88, -28.66) * mm});
            skLineSegment(sketch, "E3.10.0.20", {"start": v(-162.23, -22.31) * mm, "end": v(-162.23, -28.66) * mm});
            skLineSegment(sketch, "E3.10.0.21", {"start": v(-162.23, -22.31) * mm, "end": v(-155.88, -22.31) * mm, "construction": true});
            skLineSegment(sketch, "E3.10.0.22", {"start": v(-92.38, -22.31) * mm, "end": v(-92.38, -28.66) * mm});
            skLineSegment(sketch, "E3.10.0.24", {"start": v(-117.78, -22.31) * mm, "end": v(-117.78, -28.66) * mm});
            skLineSegment(sketch, "E3.10.0.26", {"start": v(-79.68, -22.31) * mm, "end": v(-79.68, -28.66) * mm});
            skLineSegment(sketch, "E3.10.0.27", {"start": v(-105.08, -22.31) * mm, "end": v(-105.08, -28.66) * mm});
            skLineSegment(sketch, "E3.10.0.28", {"start": v(-130.48, -22.31) * mm, "end": v(-130.48, -28.66) * mm});
            skLineSegment(sketch, "E3.10.0.30", {"start": v(-86.03, -28.66) * mm, "end": v(-79.68, -28.66) * mm});
            skLineSegment(sketch, "E3.10.0.31", {"start": v(-111.43, -28.66) * mm, "end": v(-105.08, -28.66) * mm});
            skLineSegment(sketch, "E3.10.0.32", {"start": v(-136.83, -28.66) * mm, "end": v(-130.48, -28.66) * mm});
            skLineSegment(sketch, "E3.10.0.33", {"start": v(-155.88, -22.31) * mm, "end": v(-155.88, -28.66) * mm});
            skLineSegment(sketch, "E3.10.0.34", {"start": v(-86.03, -22.31) * mm, "end": v(-86.03, -28.66) * mm});
            skLineSegment(sketch, "E3.10.0.35", {"start": v(-111.43, -22.31) * mm, "end": v(-111.43, -28.66) * mm});
            skLineSegment(sketch, "E3.10.0.36", {"start": v(-136.83, -22.31) * mm, "end": v(-136.83, -28.66) * mm});
            skLineSegment(sketch, "E3.10.0.37", {"start": v(-86.03, -22.31) * mm, "end": v(-79.68, -22.31) * mm});
            skLineSegment(sketch, "E3.10.0.38", {"start": v(-111.43, -22.31) * mm, "end": v(-105.08, -22.31) * mm});
            skLineSegment(sketch, "E3.10.0.39", {"start": v(-136.83, -22.31) * mm, "end": v(-130.48, -22.31) * mm});
            skLineSegment(sketch, "E3.10.0.40", {"start": v(-98.73, -22.31) * mm, "end": v(-98.73, -28.66) * mm});
            skLineSegment(sketch, "E3.10.0.41", {"start": v(-117.78, -22.31) * mm, "end": v(-117.78, -28.66) * mm});
            skLineSegment(sketch, "E3.10.0.42", {"start": v(-136.83, -22.31) * mm, "end": v(-136.83, -28.66) * mm});
            skLineSegment(sketch, "E3.10.0.43", {"start": v(-143.18, -22.31) * mm, "end": v(-143.18, -28.66) * mm});
            skLineSegment(sketch, "E3.10.0.44", {"start": v(-124.13, -22.31) * mm, "end": v(-124.13, -28.66) * mm});
            skLineSegment(sketch, "E3.10.0.45", {"start": v(-149.53, -22.31) * mm, "end": v(-149.53, -28.66) * mm});
            skLineSegment(sketch, "E3.10.0.46", {"start": v(-92.38, -22.31) * mm, "end": v(-92.38, -28.66) * mm});
            skLineSegment(sketch, "E3.10.0.47", {"start": v(-162.23, -22.31) * mm, "end": v(-155.88, -22.31) * mm});
            skLineSegment(sketch, "E3.10.0.48", {"start": v(-105.08, -22.31) * mm, "end": v(-105.08, -28.66) * mm});
            skLineSegment(sketch, "E3.10.0.49", {"start": v(-130.48, -22.31) * mm, "end": v(-130.48, -28.66) * mm});
            skLineSegment(sketch, "E3.10.0.50", {"start": v(-155.88, -22.31) * mm, "end": v(-155.88, -28.66) * mm});
            skLineSegment(sketch, "E3.10.0.51", {"start": v(-86.03, -22.31) * mm, "end": v(-86.03, -28.66) * mm});
            skLineSegment(sketch, "E3.10.0.52", {"start": v(-111.43, -22.31) * mm, "end": v(-111.43, -28.66) * mm});
            skLineSegment(sketch, "E3.11.0.0", {"start": v(-149.53, -28.66) * mm, "end": v(-143.18, -28.66) * mm});
            skLineSegment(sketch, "E3.11.0.3", {"start": v(-124.13, -35.01) * mm, "end": v(-117.78, -35.01) * mm});
            skLineSegment(sketch, "E3.11.0.4", {"start": v(-149.53, -35.01) * mm, "end": v(-143.18, -35.01) * mm});
            skLineSegment(sketch, "E3.11.0.5", {"start": v(-98.73, -35.01) * mm, "end": v(-92.38, -35.01) * mm});
            skLineSegment(sketch, "E3.11.0.7", {"start": v(-98.73, -28.66) * mm, "end": v(-92.38, -28.66) * mm});
            skLineSegment(sketch, "E3.11.0.8", {"start": v(-124.13, -28.66) * mm, "end": v(-117.78, -28.66) * mm});
            skLineSegment(sketch, "E3.11.0.17", {"start": v(-162.23, -35.01) * mm, "end": v(-155.88, -35.01) * mm});
            skLineSegment(sketch, "E3.11.0.21", {"start": v(-162.23, -28.66) * mm, "end": v(-155.88, -28.66) * mm, "construction": true});
            skLineSegment(sketch, "E3.11.0.30", {"start": v(-86.03, -35.01) * mm, "end": v(-79.68, -35.01) * mm});
            skLineSegment(sketch, "E3.11.0.31", {"start": v(-111.43, -35.01) * mm, "end": v(-105.08, -35.01) * mm});
            skLineSegment(sketch, "E3.11.0.32", {"start": v(-136.83, -35.01) * mm, "end": v(-130.48, -35.01) * mm});
            skLineSegment(sketch, "E3.11.0.37", {"start": v(-86.03, -28.66) * mm, "end": v(-79.68, -28.66) * mm});
            skLineSegment(sketch, "E3.11.0.38", {"start": v(-111.43, -28.66) * mm, "end": v(-105.08, -28.66) * mm});
            skLineSegment(sketch, "E3.11.0.39", {"start": v(-136.83, -28.66) * mm, "end": v(-130.48, -28.66) * mm});
            skLineSegment(sketch, "E3.11.0.47", {"start": v(-162.23, -28.66) * mm, "end": v(-155.88, -28.66) * mm});
            skLineSegment(sketch, "E3.12.0.0", {"start": v(-149.53, -35.01) * mm, "end": v(-143.18, -35.01) * mm});
            skLineSegment(sketch, "E3.12.0.1", {"start": v(-149.53, -35.01) * mm, "end": v(-149.53, -41.36) * mm});
            skLineSegment(sketch, "E3.12.0.3", {"start": v(-124.13, -41.36) * mm, "end": v(-117.78, -41.36) * mm});
            skLineSegment(sketch, "E3.12.0.4", {"start": v(-149.53, -41.36) * mm, "end": v(-143.18, -41.36) * mm});
            skLineSegment(sketch, "E3.12.0.5", {"start": v(-98.73, -41.36) * mm, "end": v(-92.38, -41.36) * mm});
            skLineSegment(sketch, "E3.12.0.7", {"start": v(-98.73, -35.01) * mm, "end": v(-92.38, -35.01) * mm});
            skLineSegment(sketch, "E3.12.0.8", {"start": v(-124.13, -35.01) * mm, "end": v(-117.78, -35.01) * mm});
            skLineSegment(sketch, "E3.12.0.11", {"start": v(-143.18, -35.01) * mm, "end": v(-143.18, -41.36) * mm});
            skLineSegment(sketch, "E3.12.0.12", {"start": v(-98.73, -35.01) * mm, "end": v(-98.73, -41.36) * mm});
            skLineSegment(sketch, "E3.12.0.13", {"start": v(-124.13, -35.01) * mm, "end": v(-124.13, -41.36) * mm});
            skLineSegment(sketch, "E3.12.0.17", {"start": v(-162.23, -41.36) * mm, "end": v(-155.88, -41.36) * mm});
            skLineSegment(sketch, "E3.12.0.20", {"start": v(-162.23, -35.01) * mm, "end": v(-162.23, -41.36) * mm});
            skLineSegment(sketch, "E3.12.0.21", {"start": v(-162.23, -35.01) * mm, "end": v(-155.88, -35.01) * mm, "construction": true});
            skLineSegment(sketch, "E3.12.0.22", {"start": v(-92.38, -35.01) * mm, "end": v(-92.38, -41.36) * mm});
            skLineSegment(sketch, "E3.12.0.24", {"start": v(-117.78, -35.01) * mm, "end": v(-117.78, -41.36) * mm});
            skLineSegment(sketch, "E3.12.0.26", {"start": v(-79.68, -35.01) * mm, "end": v(-79.68, -41.36) * mm});
            skLineSegment(sketch, "E3.12.0.27", {"start": v(-105.08, -35.01) * mm, "end": v(-105.08, -41.36) * mm});
            skLineSegment(sketch, "E3.12.0.28", {"start": v(-130.48, -35.01) * mm, "end": v(-130.48, -41.36) * mm});
            skLineSegment(sketch, "E3.12.0.30", {"start": v(-86.03, -41.36) * mm, "end": v(-79.68, -41.36) * mm});
            skLineSegment(sketch, "E3.12.0.31", {"start": v(-111.43, -41.36) * mm, "end": v(-105.08, -41.36) * mm});
            skLineSegment(sketch, "E3.12.0.32", {"start": v(-136.83, -41.36) * mm, "end": v(-130.48, -41.36) * mm});
            skLineSegment(sketch, "E3.12.0.33", {"start": v(-155.88, -35.01) * mm, "end": v(-155.88, -41.36) * mm});
            skLineSegment(sketch, "E3.12.0.34", {"start": v(-86.03, -35.01) * mm, "end": v(-86.03, -41.36) * mm});
            skLineSegment(sketch, "E3.12.0.35", {"start": v(-111.43, -35.01) * mm, "end": v(-111.43, -41.36) * mm});
            skLineSegment(sketch, "E3.12.0.36", {"start": v(-136.83, -35.01) * mm, "end": v(-136.83, -41.36) * mm});
            skLineSegment(sketch, "E3.12.0.37", {"start": v(-86.03, -35.01) * mm, "end": v(-79.68, -35.01) * mm});
            skLineSegment(sketch, "E3.12.0.38", {"start": v(-111.43, -35.01) * mm, "end": v(-105.08, -35.01) * mm});
            skLineSegment(sketch, "E3.12.0.39", {"start": v(-136.83, -35.01) * mm, "end": v(-130.48, -35.01) * mm});
            skLineSegment(sketch, "E3.12.0.40", {"start": v(-98.73, -35.01) * mm, "end": v(-98.73, -41.36) * mm});
            skLineSegment(sketch, "E3.12.0.41", {"start": v(-117.78, -35.01) * mm, "end": v(-117.78, -41.36) * mm});
            skLineSegment(sketch, "E3.12.0.42", {"start": v(-136.83, -35.01) * mm, "end": v(-136.83, -41.36) * mm});
            skLineSegment(sketch, "E3.12.0.43", {"start": v(-143.18, -35.01) * mm, "end": v(-143.18, -41.36) * mm});
            skLineSegment(sketch, "E3.12.0.44", {"start": v(-124.13, -35.01) * mm, "end": v(-124.13, -41.36) * mm});
            skLineSegment(sketch, "E3.12.0.45", {"start": v(-149.53, -35.01) * mm, "end": v(-149.53, -41.36) * mm});
            skLineSegment(sketch, "E3.12.0.46", {"start": v(-92.38, -35.01) * mm, "end": v(-92.38, -41.36) * mm});
            skLineSegment(sketch, "E3.12.0.47", {"start": v(-162.23, -35.01) * mm, "end": v(-155.88, -35.01) * mm});
            skLineSegment(sketch, "E3.12.0.48", {"start": v(-105.08, -35.01) * mm, "end": v(-105.08, -41.36) * mm});
            skLineSegment(sketch, "E3.12.0.49", {"start": v(-130.48, -35.01) * mm, "end": v(-130.48, -41.36) * mm});
            skLineSegment(sketch, "E3.12.0.50", {"start": v(-155.88, -35.01) * mm, "end": v(-155.88, -41.36) * mm});
            skLineSegment(sketch, "E3.12.0.51", {"start": v(-86.03, -35.01) * mm, "end": v(-86.03, -41.36) * mm});
            skLineSegment(sketch, "E3.12.0.52", {"start": v(-111.43, -35.01) * mm, "end": v(-111.43, -41.36) * mm});
            skLineSegment(sketch, "E3.13.0.0", {"start": v(-149.53, -41.36) * mm, "end": v(-143.18, -41.36) * mm});
            skLineSegment(sketch, "E3.13.0.3", {"start": v(-124.13, -47.71) * mm, "end": v(-117.78, -47.71) * mm});
            skLineSegment(sketch, "E3.13.0.4", {"start": v(-149.53, -47.71) * mm, "end": v(-143.18, -47.71) * mm});
            skLineSegment(sketch, "E3.13.0.5", {"start": v(-98.73, -47.71) * mm, "end": v(-92.38, -47.71) * mm});
            skLineSegment(sketch, "E3.13.0.7", {"start": v(-98.73, -41.36) * mm, "end": v(-92.38, -41.36) * mm});
            skLineSegment(sketch, "E3.13.0.8", {"start": v(-124.13, -41.36) * mm, "end": v(-117.78, -41.36) * mm});
            skLineSegment(sketch, "E3.13.0.17", {"start": v(-162.23, -47.71) * mm, "end": v(-155.88, -47.71) * mm});
            skLineSegment(sketch, "E3.13.0.21", {"start": v(-162.23, -41.36) * mm, "end": v(-155.88, -41.36) * mm, "construction": true});
            skLineSegment(sketch, "E3.13.0.30", {"start": v(-86.03, -47.71) * mm, "end": v(-79.68, -47.71) * mm});
            skLineSegment(sketch, "E3.13.0.31", {"start": v(-111.43, -47.71) * mm, "end": v(-105.08, -47.71) * mm});
            skLineSegment(sketch, "E3.13.0.32", {"start": v(-136.83, -47.71) * mm, "end": v(-130.48, -47.71) * mm});
            skLineSegment(sketch, "E3.13.0.37", {"start": v(-86.03, -41.36) * mm, "end": v(-79.68, -41.36) * mm});
            skLineSegment(sketch, "E3.13.0.38", {"start": v(-111.43, -41.36) * mm, "end": v(-105.08, -41.36) * mm});
            skLineSegment(sketch, "E3.13.0.39", {"start": v(-136.83, -41.36) * mm, "end": v(-130.48, -41.36) * mm});
            skLineSegment(sketch, "E3.13.0.47", {"start": v(-162.23, -41.36) * mm, "end": v(-155.88, -41.36) * mm});
            skLineSegment(sketch, "E3.14.0.0", {"start": v(-149.53, -47.71) * mm, "end": v(-143.18, -47.71) * mm});
            skLineSegment(sketch, "E3.14.0.1", {"start": v(-149.53, -47.71) * mm, "end": v(-149.53, -54.06) * mm});
            skLineSegment(sketch, "E3.14.0.3", {"start": v(-124.13, -54.06) * mm, "end": v(-117.78, -54.06) * mm});
            skLineSegment(sketch, "E3.14.0.4", {"start": v(-149.53, -54.06) * mm, "end": v(-143.18, -54.06) * mm});
            skLineSegment(sketch, "E3.14.0.5", {"start": v(-98.73, -54.06) * mm, "end": v(-92.38, -54.06) * mm});
            skLineSegment(sketch, "E3.14.0.7", {"start": v(-98.73, -47.71) * mm, "end": v(-92.38, -47.71) * mm});
            skLineSegment(sketch, "E3.14.0.8", {"start": v(-124.13, -47.71) * mm, "end": v(-117.78, -47.71) * mm});
            skLineSegment(sketch, "E3.14.0.11", {"start": v(-143.18, -47.71) * mm, "end": v(-143.18, -54.06) * mm});
            skLineSegment(sketch, "E3.14.0.12", {"start": v(-98.73, -47.71) * mm, "end": v(-98.73, -54.06) * mm});
            skLineSegment(sketch, "E3.14.0.13", {"start": v(-124.13, -47.71) * mm, "end": v(-124.13, -54.06) * mm});
            skLineSegment(sketch, "E3.14.0.17", {"start": v(-162.23, -54.06) * mm, "end": v(-155.88, -54.06) * mm});
            skLineSegment(sketch, "E3.14.0.20", {"start": v(-162.23, -47.71) * mm, "end": v(-162.23, -54.06) * mm});
            skLineSegment(sketch, "E3.14.0.21", {"start": v(-162.23, -47.71) * mm, "end": v(-155.88, -47.71) * mm, "construction": true});
            skLineSegment(sketch, "E3.14.0.22", {"start": v(-92.38, -47.71) * mm, "end": v(-92.38, -54.06) * mm});
            skLineSegment(sketch, "E3.14.0.24", {"start": v(-117.78, -47.71) * mm, "end": v(-117.78, -54.06) * mm});
            skLineSegment(sketch, "E3.14.0.26", {"start": v(-79.68, -47.71) * mm, "end": v(-79.68, -54.06) * mm});
            skLineSegment(sketch, "E3.14.0.27", {"start": v(-105.08, -47.71) * mm, "end": v(-105.08, -54.06) * mm});
            skLineSegment(sketch, "E3.14.0.28", {"start": v(-130.48, -47.71) * mm, "end": v(-130.48, -54.06) * mm});
            skLineSegment(sketch, "E3.14.0.30", {"start": v(-86.03, -54.06) * mm, "end": v(-79.68, -54.06) * mm});
            skLineSegment(sketch, "E3.14.0.31", {"start": v(-111.43, -54.06) * mm, "end": v(-105.08, -54.06) * mm});
            skLineSegment(sketch, "E3.14.0.32", {"start": v(-136.83, -54.06) * mm, "end": v(-130.48, -54.06) * mm});
            skLineSegment(sketch, "E3.14.0.33", {"start": v(-155.88, -47.71) * mm, "end": v(-155.88, -54.06) * mm});
            skLineSegment(sketch, "E3.14.0.34", {"start": v(-86.03, -47.71) * mm, "end": v(-86.03, -54.06) * mm});
            skLineSegment(sketch, "E3.14.0.35", {"start": v(-111.43, -47.71) * mm, "end": v(-111.43, -54.06) * mm});
            skLineSegment(sketch, "E3.14.0.36", {"start": v(-136.83, -47.71) * mm, "end": v(-136.83, -54.06) * mm});
            skLineSegment(sketch, "E3.14.0.37", {"start": v(-86.03, -47.71) * mm, "end": v(-79.68, -47.71) * mm});
            skLineSegment(sketch, "E3.14.0.38", {"start": v(-111.43, -47.71) * mm, "end": v(-105.08, -47.71) * mm});
            skLineSegment(sketch, "E3.14.0.39", {"start": v(-136.83, -47.71) * mm, "end": v(-130.48, -47.71) * mm});
            skLineSegment(sketch, "E3.14.0.40", {"start": v(-98.73, -47.71) * mm, "end": v(-98.73, -54.06) * mm});
            skLineSegment(sketch, "E3.14.0.41", {"start": v(-117.78, -47.71) * mm, "end": v(-117.78, -54.06) * mm});
            skLineSegment(sketch, "E3.14.0.42", {"start": v(-136.83, -47.71) * mm, "end": v(-136.83, -54.06) * mm});
            skLineSegment(sketch, "E3.14.0.43", {"start": v(-143.18, -47.71) * mm, "end": v(-143.18, -54.06) * mm});
            skLineSegment(sketch, "E3.14.0.44", {"start": v(-124.13, -47.71) * mm, "end": v(-124.13, -54.06) * mm});
            skLineSegment(sketch, "E3.14.0.45", {"start": v(-149.53, -47.71) * mm, "end": v(-149.53, -54.06) * mm});
            skLineSegment(sketch, "E3.14.0.46", {"start": v(-92.38, -47.71) * mm, "end": v(-92.38, -54.06) * mm});
            skLineSegment(sketch, "E3.14.0.47", {"start": v(-162.23, -47.71) * mm, "end": v(-155.88, -47.71) * mm});
            skLineSegment(sketch, "E3.14.0.48", {"start": v(-105.08, -47.71) * mm, "end": v(-105.08, -54.06) * mm});
            skLineSegment(sketch, "E3.14.0.49", {"start": v(-130.48, -47.71) * mm, "end": v(-130.48, -54.06) * mm});
            skLineSegment(sketch, "E3.14.0.50", {"start": v(-155.88, -47.71) * mm, "end": v(-155.88, -54.06) * mm});
            skLineSegment(sketch, "E3.14.0.51", {"start": v(-86.03, -47.71) * mm, "end": v(-86.03, -54.06) * mm});
            skLineSegment(sketch, "E3.14.0.52", {"start": v(-111.43, -47.71) * mm, "end": v(-111.43, -54.06) * mm});
            skLineSegment(sketch, "E3.15.0.0", {"start": v(-149.53, -54.06) * mm, "end": v(-143.18, -54.06) * mm});
            skLineSegment(sketch, "E3.15.0.3", {"start": v(-124.13, -60.41) * mm, "end": v(-117.78, -60.41) * mm});
            skLineSegment(sketch, "E3.15.0.4", {"start": v(-149.53, -60.41) * mm, "end": v(-143.18, -60.41) * mm});
            skLineSegment(sketch, "E3.15.0.5", {"start": v(-98.73, -60.41) * mm, "end": v(-92.38, -60.41) * mm});
            skLineSegment(sketch, "E3.15.0.7", {"start": v(-98.73, -54.06) * mm, "end": v(-92.38, -54.06) * mm});
            skLineSegment(sketch, "E3.15.0.8", {"start": v(-124.13, -54.06) * mm, "end": v(-117.78, -54.06) * mm});
            skLineSegment(sketch, "E3.15.0.17", {"start": v(-162.23, -60.41) * mm, "end": v(-155.88, -60.41) * mm});
            skLineSegment(sketch, "E3.15.0.21", {"start": v(-162.23, -54.06) * mm, "end": v(-155.88, -54.06) * mm, "construction": true});
            skLineSegment(sketch, "E3.15.0.30", {"start": v(-86.03, -60.41) * mm, "end": v(-79.68, -60.41) * mm});
            skLineSegment(sketch, "E3.15.0.31", {"start": v(-111.43, -60.41) * mm, "end": v(-105.08, -60.41) * mm});
            skLineSegment(sketch, "E3.15.0.32", {"start": v(-136.83, -60.41) * mm, "end": v(-130.48, -60.41) * mm});
            skLineSegment(sketch, "E3.15.0.37", {"start": v(-86.03, -54.06) * mm, "end": v(-79.68, -54.06) * mm});
            skLineSegment(sketch, "E3.15.0.38", {"start": v(-111.43, -54.06) * mm, "end": v(-105.08, -54.06) * mm});
            skLineSegment(sketch, "E3.15.0.39", {"start": v(-136.83, -54.06) * mm, "end": v(-130.48, -54.06) * mm});
            skLineSegment(sketch, "E3.15.0.47", {"start": v(-162.23, -54.06) * mm, "end": v(-155.88, -54.06) * mm});
            skLineSegment(sketch, "E3.16.0.0", {"start": v(-149.53, -60.41) * mm, "end": v(-143.18, -60.41) * mm});
            skLineSegment(sketch, "E3.16.0.1", {"start": v(-149.53, -60.41) * mm, "end": v(-149.53, -66.76) * mm});
            skLineSegment(sketch, "E3.16.0.3", {"start": v(-124.13, -66.76) * mm, "end": v(-117.78, -66.76) * mm});
            skLineSegment(sketch, "E3.16.0.4", {"start": v(-149.53, -66.76) * mm, "end": v(-143.18, -66.76) * mm});
            skLineSegment(sketch, "E3.16.0.5", {"start": v(-98.73, -66.76) * mm, "end": v(-92.38, -66.76) * mm});
            skLineSegment(sketch, "E3.16.0.7", {"start": v(-98.73, -60.41) * mm, "end": v(-92.38, -60.41) * mm});
            skLineSegment(sketch, "E3.16.0.8", {"start": v(-124.13, -60.41) * mm, "end": v(-117.78, -60.41) * mm});
            skLineSegment(sketch, "E3.16.0.11", {"start": v(-143.18, -60.41) * mm, "end": v(-143.18, -66.76) * mm});
            skLineSegment(sketch, "E3.16.0.12", {"start": v(-98.73, -60.41) * mm, "end": v(-98.73, -66.76) * mm});
            skLineSegment(sketch, "E3.16.0.13", {"start": v(-124.13, -60.41) * mm, "end": v(-124.13, -66.76) * mm});
            skLineSegment(sketch, "E3.16.0.17", {"start": v(-162.23, -66.76) * mm, "end": v(-155.88, -66.76) * mm});
            skLineSegment(sketch, "E3.16.0.20", {"start": v(-162.23, -60.41) * mm, "end": v(-162.23, -66.76) * mm});
            skLineSegment(sketch, "E3.16.0.21", {"start": v(-162.23, -60.41) * mm, "end": v(-155.88, -60.41) * mm, "construction": true});
            skLineSegment(sketch, "E3.16.0.22", {"start": v(-92.38, -60.41) * mm, "end": v(-92.38, -66.76) * mm});
            skLineSegment(sketch, "E3.16.0.24", {"start": v(-117.78, -60.41) * mm, "end": v(-117.78, -66.76) * mm});
            skLineSegment(sketch, "E3.16.0.26", {"start": v(-79.68, -60.41) * mm, "end": v(-79.68, -66.76) * mm});
            skLineSegment(sketch, "E3.16.0.27", {"start": v(-105.08, -60.41) * mm, "end": v(-105.08, -66.76) * mm});
            skLineSegment(sketch, "E3.16.0.28", {"start": v(-130.48, -60.41) * mm, "end": v(-130.48, -66.76) * mm});
            skLineSegment(sketch, "E3.16.0.30", {"start": v(-86.03, -66.76) * mm, "end": v(-79.68, -66.76) * mm});
            skLineSegment(sketch, "E3.16.0.31", {"start": v(-111.43, -66.76) * mm, "end": v(-105.08, -66.76) * mm});
            skLineSegment(sketch, "E3.16.0.32", {"start": v(-136.83, -66.76) * mm, "end": v(-130.48, -66.76) * mm});
            skLineSegment(sketch, "E3.16.0.33", {"start": v(-155.88, -60.41) * mm, "end": v(-155.88, -66.76) * mm});
            skLineSegment(sketch, "E3.16.0.34", {"start": v(-86.03, -60.41) * mm, "end": v(-86.03, -66.76) * mm});
            skLineSegment(sketch, "E3.16.0.35", {"start": v(-111.43, -60.41) * mm, "end": v(-111.43, -66.76) * mm});
            skLineSegment(sketch, "E3.16.0.36", {"start": v(-136.83, -60.41) * mm, "end": v(-136.83, -66.76) * mm});
            skLineSegment(sketch, "E3.16.0.37", {"start": v(-86.03, -60.41) * mm, "end": v(-79.68, -60.41) * mm});
            skLineSegment(sketch, "E3.16.0.38", {"start": v(-111.43, -60.41) * mm, "end": v(-105.08, -60.41) * mm});
            skLineSegment(sketch, "E3.16.0.39", {"start": v(-136.83, -60.41) * mm, "end": v(-130.48, -60.41) * mm});
            skLineSegment(sketch, "E3.16.0.40", {"start": v(-98.73, -60.41) * mm, "end": v(-98.73, -66.76) * mm});
            skLineSegment(sketch, "E3.16.0.41", {"start": v(-117.78, -60.41) * mm, "end": v(-117.78, -66.76) * mm});
            skLineSegment(sketch, "E3.16.0.42", {"start": v(-136.83, -60.41) * mm, "end": v(-136.83, -66.76) * mm});
            skLineSegment(sketch, "E3.16.0.43", {"start": v(-143.18, -60.41) * mm, "end": v(-143.18, -66.76) * mm});
            skLineSegment(sketch, "E3.16.0.44", {"start": v(-124.13, -60.41) * mm, "end": v(-124.13, -66.76) * mm});
            skLineSegment(sketch, "E3.16.0.45", {"start": v(-149.53, -60.41) * mm, "end": v(-149.53, -66.76) * mm});
            skLineSegment(sketch, "E3.16.0.46", {"start": v(-92.38, -60.41) * mm, "end": v(-92.38, -66.76) * mm});
            skLineSegment(sketch, "E3.16.0.47", {"start": v(-162.23, -60.41) * mm, "end": v(-155.88, -60.41) * mm});
            skLineSegment(sketch, "E3.16.0.48", {"start": v(-105.08, -60.41) * mm, "end": v(-105.08, -66.76) * mm});
            skLineSegment(sketch, "E3.16.0.49", {"start": v(-130.48, -60.41) * mm, "end": v(-130.48, -66.76) * mm});
            skLineSegment(sketch, "E3.16.0.50", {"start": v(-155.88, -60.41) * mm, "end": v(-155.88, -66.76) * mm});
            skLineSegment(sketch, "E3.16.0.51", {"start": v(-86.03, -60.41) * mm, "end": v(-86.03, -66.76) * mm});
            skLineSegment(sketch, "E3.16.0.52", {"start": v(-111.43, -60.41) * mm, "end": v(-111.43, -66.76) * mm});
            skLineSegment(sketch, "E3.17.0.0", {"start": v(-149.53, -66.76) * mm, "end": v(-143.18, -66.76) * mm});
            skLineSegment(sketch, "E3.17.0.3", {"start": v(-124.13, -73.11) * mm, "end": v(-117.78, -73.11) * mm});
            skLineSegment(sketch, "E3.17.0.4", {"start": v(-149.53, -73.11) * mm, "end": v(-143.18, -73.11) * mm});
            skLineSegment(sketch, "E3.17.0.5", {"start": v(-98.73, -73.11) * mm, "end": v(-92.38, -73.11) * mm});
            skLineSegment(sketch, "E3.17.0.7", {"start": v(-98.73, -66.76) * mm, "end": v(-92.38, -66.76) * mm});
            skLineSegment(sketch, "E3.17.0.8", {"start": v(-124.13, -66.76) * mm, "end": v(-117.78, -66.76) * mm});
            skLineSegment(sketch, "E3.17.0.17", {"start": v(-162.23, -73.11) * mm, "end": v(-155.88, -73.11) * mm});
            skLineSegment(sketch, "E3.17.0.21", {"start": v(-162.23, -66.76) * mm, "end": v(-155.88, -66.76) * mm, "construction": true});
            skLineSegment(sketch, "E3.17.0.30", {"start": v(-86.03, -73.11) * mm, "end": v(-79.68, -73.11) * mm});
            skLineSegment(sketch, "E3.17.0.31", {"start": v(-111.43, -73.11) * mm, "end": v(-105.08, -73.11) * mm});
            skLineSegment(sketch, "E3.17.0.32", {"start": v(-136.83, -73.11) * mm, "end": v(-130.48, -73.11) * mm});
            skLineSegment(sketch, "E3.17.0.37", {"start": v(-86.03, -66.76) * mm, "end": v(-79.68, -66.76) * mm});
            skLineSegment(sketch, "E3.17.0.38", {"start": v(-111.43, -66.76) * mm, "end": v(-105.08, -66.76) * mm});
            skLineSegment(sketch, "E3.17.0.39", {"start": v(-136.83, -66.76) * mm, "end": v(-130.48, -66.76) * mm});
            skLineSegment(sketch, "E3.17.0.47", {"start": v(-162.23, -66.76) * mm, "end": v(-155.88, -66.76) * mm});
            skLineSegment(sketch, "E3.18.0.0", {"start": v(-149.53, -73.11) * mm, "end": v(-143.18, -73.11) * mm});
            skLineSegment(sketch, "E3.18.0.1", {"start": v(-149.53, -73.11) * mm, "end": v(-149.53, -79.46) * mm});
            skLineSegment(sketch, "E3.18.0.3", {"start": v(-124.13, -79.46) * mm, "end": v(-117.78, -79.46) * mm});
            skLineSegment(sketch, "E3.18.0.4", {"start": v(-149.53, -79.46) * mm, "end": v(-143.18, -79.46) * mm});
            skLineSegment(sketch, "E3.18.0.5", {"start": v(-98.73, -79.46) * mm, "end": v(-92.38, -79.46) * mm});
            skLineSegment(sketch, "E3.18.0.7", {"start": v(-98.73, -73.11) * mm, "end": v(-92.38, -73.11) * mm});
            skLineSegment(sketch, "E3.18.0.8", {"start": v(-124.13, -73.11) * mm, "end": v(-117.78, -73.11) * mm});
            skLineSegment(sketch, "E3.18.0.11", {"start": v(-143.18, -73.11) * mm, "end": v(-143.18, -79.46) * mm});
            skLineSegment(sketch, "E3.18.0.12", {"start": v(-98.73, -73.11) * mm, "end": v(-98.73, -79.46) * mm});
            skLineSegment(sketch, "E3.18.0.13", {"start": v(-124.13, -73.11) * mm, "end": v(-124.13, -79.46) * mm});
            skLineSegment(sketch, "E3.18.0.17", {"start": v(-162.23, -79.46) * mm, "end": v(-155.88, -79.46) * mm});
            skLineSegment(sketch, "E3.18.0.20", {"start": v(-162.23, -73.11) * mm, "end": v(-162.23, -79.46) * mm});
            skLineSegment(sketch, "E3.18.0.21", {"start": v(-162.23, -73.11) * mm, "end": v(-155.88, -73.11) * mm, "construction": true});
            skLineSegment(sketch, "E3.18.0.22", {"start": v(-92.38, -73.11) * mm, "end": v(-92.38, -79.46) * mm});
            skLineSegment(sketch, "E3.18.0.24", {"start": v(-117.78, -73.11) * mm, "end": v(-117.78, -79.46) * mm});
            skLineSegment(sketch, "E3.18.0.26", {"start": v(-79.68, -73.11) * mm, "end": v(-79.68, -79.46) * mm});
            skLineSegment(sketch, "E3.18.0.27", {"start": v(-105.08, -73.11) * mm, "end": v(-105.08, -79.46) * mm});
            skLineSegment(sketch, "E3.18.0.28", {"start": v(-130.48, -73.11) * mm, "end": v(-130.48, -79.46) * mm});
            skLineSegment(sketch, "E3.18.0.30", {"start": v(-86.03, -79.46) * mm, "end": v(-79.68, -79.46) * mm});
            skLineSegment(sketch, "E3.18.0.31", {"start": v(-111.43, -79.46) * mm, "end": v(-105.08, -79.46) * mm});
            skLineSegment(sketch, "E3.18.0.32", {"start": v(-136.83, -79.46) * mm, "end": v(-130.48, -79.46) * mm});
            skLineSegment(sketch, "E3.18.0.33", {"start": v(-155.88, -73.11) * mm, "end": v(-155.88, -79.46) * mm});
            skLineSegment(sketch, "E3.18.0.34", {"start": v(-86.03, -73.11) * mm, "end": v(-86.03, -79.46) * mm});
            skLineSegment(sketch, "E3.18.0.35", {"start": v(-111.43, -73.11) * mm, "end": v(-111.43, -79.46) * mm});
            skLineSegment(sketch, "E3.18.0.36", {"start": v(-136.83, -73.11) * mm, "end": v(-136.83, -79.46) * mm});
            skLineSegment(sketch, "E3.18.0.37", {"start": v(-86.03, -73.11) * mm, "end": v(-79.68, -73.11) * mm});
            skLineSegment(sketch, "E3.18.0.38", {"start": v(-111.43, -73.11) * mm, "end": v(-105.08, -73.11) * mm});
            skLineSegment(sketch, "E3.18.0.39", {"start": v(-136.83, -73.11) * mm, "end": v(-130.48, -73.11) * mm});
            skLineSegment(sketch, "E3.18.0.40", {"start": v(-98.73, -73.11) * mm, "end": v(-98.73, -79.46) * mm});
            skLineSegment(sketch, "E3.18.0.41", {"start": v(-117.78, -73.11) * mm, "end": v(-117.78, -79.46) * mm});
            skLineSegment(sketch, "E3.18.0.42", {"start": v(-136.83, -73.11) * mm, "end": v(-136.83, -79.46) * mm});
            skLineSegment(sketch, "E3.18.0.43", {"start": v(-143.18, -73.11) * mm, "end": v(-143.18, -79.46) * mm});
            skLineSegment(sketch, "E3.18.0.44", {"start": v(-124.13, -73.11) * mm, "end": v(-124.13, -79.46) * mm});
            skLineSegment(sketch, "E3.18.0.45", {"start": v(-149.53, -73.11) * mm, "end": v(-149.53, -79.46) * mm});
            skLineSegment(sketch, "E3.18.0.46", {"start": v(-92.38, -73.11) * mm, "end": v(-92.38, -79.46) * mm});
            skLineSegment(sketch, "E3.18.0.47", {"start": v(-162.23, -73.11) * mm, "end": v(-155.88, -73.11) * mm});
            skLineSegment(sketch, "E3.18.0.48", {"start": v(-105.08, -73.11) * mm, "end": v(-105.08, -79.46) * mm});
            skLineSegment(sketch, "E3.18.0.49", {"start": v(-130.48, -73.11) * mm, "end": v(-130.48, -79.46) * mm});
            skLineSegment(sketch, "E3.18.0.50", {"start": v(-155.88, -73.11) * mm, "end": v(-155.88, -79.46) * mm});
            skLineSegment(sketch, "E3.18.0.51", {"start": v(-86.03, -73.11) * mm, "end": v(-86.03, -79.46) * mm});
            skLineSegment(sketch, "E3.18.0.52", {"start": v(-111.43, -73.11) * mm, "end": v(-111.43, -79.46) * mm});
            skLineSegment(sketch, "E3.19.0.0", {"start": v(-149.53, -79.46) * mm, "end": v(-143.18, -79.46) * mm});
            skLineSegment(sketch, "E3.19.0.3", {"start": v(-124.13, -85.81) * mm, "end": v(-117.78, -85.81) * mm});
            skLineSegment(sketch, "E3.19.0.4", {"start": v(-149.53, -85.81) * mm, "end": v(-143.18, -85.81) * mm});
            skLineSegment(sketch, "E3.19.0.5", {"start": v(-98.73, -85.81) * mm, "end": v(-92.38, -85.81) * mm});
            skLineSegment(sketch, "E3.19.0.7", {"start": v(-98.73, -79.46) * mm, "end": v(-92.38, -79.46) * mm});
            skLineSegment(sketch, "E3.19.0.8", {"start": v(-124.13, -79.46) * mm, "end": v(-117.78, -79.46) * mm});
            skLineSegment(sketch, "E3.19.0.17", {"start": v(-162.23, -85.81) * mm, "end": v(-155.88, -85.81) * mm});
            skLineSegment(sketch, "E3.19.0.21", {"start": v(-162.23, -79.46) * mm, "end": v(-155.88, -79.46) * mm, "construction": true});
            skLineSegment(sketch, "E3.19.0.30", {"start": v(-86.03, -85.81) * mm, "end": v(-79.68, -85.81) * mm});
            skLineSegment(sketch, "E3.19.0.31", {"start": v(-111.43, -85.81) * mm, "end": v(-105.08, -85.81) * mm});
            skLineSegment(sketch, "E3.19.0.32", {"start": v(-136.83, -85.81) * mm, "end": v(-130.48, -85.81) * mm});
            skLineSegment(sketch, "E3.19.0.37", {"start": v(-86.03, -79.46) * mm, "end": v(-79.68, -79.46) * mm});
            skLineSegment(sketch, "E3.19.0.38", {"start": v(-111.43, -79.46) * mm, "end": v(-105.08, -79.46) * mm});
            skLineSegment(sketch, "E3.19.0.39", {"start": v(-136.83, -79.46) * mm, "end": v(-130.48, -79.46) * mm});
            skLineSegment(sketch, "E3.19.0.47", {"start": v(-162.23, -79.46) * mm, "end": v(-155.88, -79.46) * mm});
            skLineSegment(sketch, "E3.20.0.0", {"start": v(-149.53, -85.81) * mm, "end": v(-143.18, -85.81) * mm});
            skLineSegment(sketch, "E3.20.0.1", {"start": v(-149.53, -85.81) * mm, "end": v(-149.53, -92.16) * mm});
            skLineSegment(sketch, "E3.20.0.3", {"start": v(-124.13, -92.16) * mm, "end": v(-117.78, -92.16) * mm});
            skLineSegment(sketch, "E3.20.0.4", {"start": v(-149.53, -92.16) * mm, "end": v(-143.18, -92.16) * mm});
            skLineSegment(sketch, "E3.20.0.5", {"start": v(-98.73, -92.16) * mm, "end": v(-92.38, -92.16) * mm});
            skLineSegment(sketch, "E3.20.0.7", {"start": v(-98.73, -85.81) * mm, "end": v(-92.38, -85.81) * mm});
            skLineSegment(sketch, "E3.20.0.8", {"start": v(-124.13, -85.81) * mm, "end": v(-117.78, -85.81) * mm});
            skLineSegment(sketch, "E3.20.0.11", {"start": v(-143.18, -85.81) * mm, "end": v(-143.18, -92.16) * mm});
            skLineSegment(sketch, "E3.20.0.12", {"start": v(-98.73, -85.81) * mm, "end": v(-98.73, -92.16) * mm});
            skLineSegment(sketch, "E3.20.0.13", {"start": v(-124.13, -85.81) * mm, "end": v(-124.13, -92.16) * mm});
            skLineSegment(sketch, "E3.20.0.17", {"start": v(-162.23, -92.16) * mm, "end": v(-155.88, -92.16) * mm});
            skLineSegment(sketch, "E3.20.0.20", {"start": v(-162.23, -85.81) * mm, "end": v(-162.23, -92.16) * mm});
            skLineSegment(sketch, "E3.20.0.21", {"start": v(-162.23, -85.81) * mm, "end": v(-155.88, -85.81) * mm, "construction": true});
            skLineSegment(sketch, "E3.20.0.22", {"start": v(-92.38, -85.81) * mm, "end": v(-92.38, -92.16) * mm});
            skLineSegment(sketch, "E3.20.0.24", {"start": v(-117.78, -85.81) * mm, "end": v(-117.78, -92.16) * mm});
            skLineSegment(sketch, "E3.20.0.26", {"start": v(-79.68, -85.81) * mm, "end": v(-79.68, -92.16) * mm});
            skLineSegment(sketch, "E3.20.0.27", {"start": v(-105.08, -85.81) * mm, "end": v(-105.08, -92.16) * mm});
            skLineSegment(sketch, "E3.20.0.28", {"start": v(-130.48, -85.81) * mm, "end": v(-130.48, -92.16) * mm});
            skLineSegment(sketch, "E3.20.0.30", {"start": v(-86.03, -92.16) * mm, "end": v(-79.68, -92.16) * mm});
            skLineSegment(sketch, "E3.20.0.31", {"start": v(-111.43, -92.16) * mm, "end": v(-105.08, -92.16) * mm});
            skLineSegment(sketch, "E3.20.0.32", {"start": v(-136.83, -92.16) * mm, "end": v(-130.48, -92.16) * mm});
            skLineSegment(sketch, "E3.20.0.33", {"start": v(-155.88, -85.81) * mm, "end": v(-155.88, -92.16) * mm});
            skLineSegment(sketch, "E3.20.0.34", {"start": v(-86.03, -85.81) * mm, "end": v(-86.03, -92.16) * mm});
            skLineSegment(sketch, "E3.20.0.35", {"start": v(-111.43, -85.81) * mm, "end": v(-111.43, -92.16) * mm});
            skLineSegment(sketch, "E3.20.0.36", {"start": v(-136.83, -85.81) * mm, "end": v(-136.83, -92.16) * mm});
            skLineSegment(sketch, "E3.20.0.37", {"start": v(-86.03, -85.81) * mm, "end": v(-79.68, -85.81) * mm});
            skLineSegment(sketch, "E3.20.0.38", {"start": v(-111.43, -85.81) * mm, "end": v(-105.08, -85.81) * mm});
            skLineSegment(sketch, "E3.20.0.39", {"start": v(-136.83, -85.81) * mm, "end": v(-130.48, -85.81) * mm});
            skLineSegment(sketch, "E3.20.0.40", {"start": v(-98.73, -85.81) * mm, "end": v(-98.73, -92.16) * mm});
            skLineSegment(sketch, "E3.20.0.41", {"start": v(-117.78, -85.81) * mm, "end": v(-117.78, -92.16) * mm});
            skLineSegment(sketch, "E3.20.0.42", {"start": v(-136.83, -85.81) * mm, "end": v(-136.83, -92.16) * mm});
            skLineSegment(sketch, "E3.20.0.43", {"start": v(-143.18, -85.81) * mm, "end": v(-143.18, -92.16) * mm});
            skLineSegment(sketch, "E3.20.0.44", {"start": v(-124.13, -85.81) * mm, "end": v(-124.13, -92.16) * mm});
            skLineSegment(sketch, "E3.20.0.45", {"start": v(-149.53, -85.81) * mm, "end": v(-149.53, -92.16) * mm});
            skLineSegment(sketch, "E3.20.0.46", {"start": v(-92.38, -85.81) * mm, "end": v(-92.38, -92.16) * mm});
            skLineSegment(sketch, "E3.20.0.47", {"start": v(-162.23, -85.81) * mm, "end": v(-155.88, -85.81) * mm});
            skLineSegment(sketch, "E3.20.0.48", {"start": v(-105.08, -85.81) * mm, "end": v(-105.08, -92.16) * mm});
            skLineSegment(sketch, "E3.20.0.49", {"start": v(-130.48, -85.81) * mm, "end": v(-130.48, -92.16) * mm});
            skLineSegment(sketch, "E3.20.0.50", {"start": v(-155.88, -85.81) * mm, "end": v(-155.88, -92.16) * mm});
            skLineSegment(sketch, "E3.20.0.51", {"start": v(-86.03, -85.81) * mm, "end": v(-86.03, -92.16) * mm});
            skLineSegment(sketch, "E3.20.0.52", {"start": v(-111.43, -85.81) * mm, "end": v(-111.43, -92.16) * mm});
            skSolve(sketch);
        }
        {
            var Q0;
            Q0=makeQuery(id+"F2.imprint","IMPRINT",FACE,{"disambiguationData":[TD([[makeQuery(id+"F2.imprint","IMPRINT",EDGE,{"derivedFrom":sQuery(id+"F2.wireOp",EDGE,"E1.bottom")}),-1.0]])]});
            var Q1;
            Q1=makeQuery(id+"F2.imprint","IMPRINT",FACE,{"disambiguationData":[TD([[makeQuery(id+"F2.imprint","IMPRINT",EDGE,{"derivedFrom":sQuery(id+"F2.wireOp",EDGE,"E2.2.0.0")}),-1.0]])]});
            var Q2;
            Q2=makeQuery(id+"F2.imprint","IMPRINT",FACE,{"disambiguationData":[TD([[makeQuery(id+"F2.imprint","IMPRINT",EDGE,{"derivedFrom":sQuery(id+"F2.wireOp",EDGE,"E2.4.0.0")}),-1.0]])]});
            var Q3;
            Q3=makeQuery(id+"F2.imprint","IMPRINT",FACE,{"disambiguationData":[TD([[makeQuery(id+"F2.imprint","IMPRINT",EDGE,{"derivedFrom":sQuery(id+"F2.wireOp",EDGE,"E2.6.0.0")}),-1.0]])]});
            var Q4;
            Q4=makeQuery(id+"F2.imprint","IMPRINT",FACE,{"disambiguationData":[TD([[makeQuery(id+"F2.imprint","IMPRINT",EDGE,{"derivedFrom":sQuery(id+"F2.wireOp",EDGE,"E2.8.0.0")}),-1.0]])]});
            var Q5;
            Q5=makeQuery(id+"F2.imprint","IMPRINT",FACE,{"disambiguationData":[TD([[makeQuery(id+"F2.imprint","IMPRINT",EDGE,{"derivedFrom":sQuery(id+"F2.wireOp",EDGE,"E2.10.0.0")}),-1.0]])]});
            var Q6;
            Q6=makeQuery(id+"F2.imprint","IMPRINT",FACE,{"disambiguationData":[TD([[makeQuery(id+"F2.imprint","IMPRINT",EDGE,{"derivedFrom":sQuery(id+"F2.wireOp",EDGE,"E2.12.0.0")}),-1.0]])]});
            var Q7;
            Q7=makeQuery(id+"F2.imprint","IMPRINT",FACE,{"disambiguationData":[TD([[makeQuery(id+"F2.imprint","IMPRINT",EDGE,{"derivedFrom":sQuery(id+"F2.wireOp",EDGE,"E3.2.0.8")}),-1.0]])]});
            var Q8;
            Q8=makeQuery(id+"F2.imprint","IMPRINT",FACE,{"disambiguationData":[TD([[makeQuery(id+"F2.imprint","IMPRINT",EDGE,{"derivedFrom":sQuery(id+"F2.wireOp",EDGE,"E3.2.0.20")}),1.0]])]});
            var Q9;
            Q9=makeQuery(id+"F2.imprint","IMPRINT",FACE,{"disambiguationData":[TD([[makeQuery(id+"F2.imprint","IMPRINT",EDGE,{"derivedFrom":sQuery(id+"F2.wireOp",EDGE,"E3.2.0.0")}),-1.0]])]});
            var Q10;
            Q10=makeQuery(id+"F2.imprint","IMPRINT",FACE,{"disambiguationData":[TD([[makeQuery(id+"F2.imprint","IMPRINT",EDGE,{"derivedFrom":sQuery(id+"F2.wireOp",EDGE,"E3.2.0.39")}),-1.0]])]});
            var Q11;
            Q11=makeQuery(id+"F2.imprint","IMPRINT",FACE,{"disambiguationData":[TD([[makeQuery(id+"F2.imprint","IMPRINT",EDGE,{"derivedFrom":sQuery(id+"F2.wireOp",EDGE,"E3.2.0.38")}),-1.0]])]});
            var Q12;
            Q12=makeQuery(id+"F2.imprint","IMPRINT",FACE,{"disambiguationData":[TD([[makeQuery(id+"F2.imprint","IMPRINT",EDGE,{"derivedFrom":sQuery(id+"F2.wireOp",EDGE,"E3.2.0.7")}),-1.0]])]});
            var Q13;
            Q13=makeQuery(id+"F2.imprint","IMPRINT",FACE,{"disambiguationData":[TD([[makeQuery(id+"F2.imprint","IMPRINT",EDGE,{"derivedFrom":sQuery(id+"F2.wireOp",EDGE,"E3.2.0.26")}),-1.0]])]});
            var Q14;
            Q14=makeQuery(id+"F2.imprint","IMPRINT",FACE,{"disambiguationData":[TD([[makeQuery(id+"F2.imprint","IMPRINT",EDGE,{"derivedFrom":sQuery(id+"F2.wireOp",EDGE,"E3.4.0.26")}),-1.0]])]});
            var Q15;
            Q15=makeQuery(id+"F2.imprint","IMPRINT",FACE,{"disambiguationData":[TD([[makeQuery(id+"F2.imprint","IMPRINT",EDGE,{"derivedFrom":sQuery(id+"F2.wireOp",EDGE,"E3.4.0.7")}),-1.0]])]});
            var Q16;
            Q16=makeQuery(id+"F2.imprint","IMPRINT",FACE,{"disambiguationData":[TD([[makeQuery(id+"F2.imprint","IMPRINT",EDGE,{"derivedFrom":sQuery(id+"F2.wireOp",EDGE,"E3.4.0.38")}),-1.0]])]});
            var Q17;
            Q17=makeQuery(id+"F2.imprint","IMPRINT",FACE,{"disambiguationData":[TD([[makeQuery(id+"F2.imprint","IMPRINT",EDGE,{"derivedFrom":sQuery(id+"F2.wireOp",EDGE,"E3.4.0.8")}),-1.0]])]});
            var Q18;
            Q18=makeQuery(id+"F2.imprint","IMPRINT",FACE,{"disambiguationData":[TD([[makeQuery(id+"F2.imprint","IMPRINT",EDGE,{"derivedFrom":sQuery(id+"F2.wireOp",EDGE,"E3.4.0.39")}),-1.0]])]});
            var Q19;
            Q19=makeQuery(id+"F2.imprint","IMPRINT",FACE,{"disambiguationData":[TD([[makeQuery(id+"F2.imprint","IMPRINT",EDGE,{"derivedFrom":sQuery(id+"F2.wireOp",EDGE,"E3.4.0.0")}),-1.0]])]});
            var Q20;
            Q20=makeQuery(id+"F2.imprint","IMPRINT",FACE,{"disambiguationData":[TD([[makeQuery(id+"F2.imprint","IMPRINT",EDGE,{"derivedFrom":sQuery(id+"F2.wireOp",EDGE,"E3.4.0.20")}),1.0]])]});
            var Q21;
            Q21=makeQuery(id+"F2.imprint","IMPRINT",FACE,{"disambiguationData":[TD([[makeQuery(id+"F2.imprint","IMPRINT",EDGE,{"derivedFrom":sQuery(id+"F2.wireOp",EDGE,"E3.6.0.20")}),1.0]])]});
            var Q22;
            Q22=makeQuery(id+"F2.imprint","IMPRINT",FACE,{"disambiguationData":[TD([[makeQuery(id+"F2.imprint","IMPRINT",EDGE,{"derivedFrom":sQuery(id+"F2.wireOp",EDGE,"E3.6.0.0")}),-1.0]])]});
            var Q23;
            Q23=makeQuery(id+"F2.imprint","IMPRINT",FACE,{"disambiguationData":[TD([[makeQuery(id+"F2.imprint","IMPRINT",EDGE,{"derivedFrom":sQuery(id+"F2.wireOp",EDGE,"E3.6.0.39")}),-1.0]])]});
            var Q24;
            Q24=makeQuery(id+"F2.imprint","IMPRINT",FACE,{"disambiguationData":[TD([[makeQuery(id+"F2.imprint","IMPRINT",EDGE,{"derivedFrom":sQuery(id+"F2.wireOp",EDGE,"E3.6.0.8")}),-1.0]])]});
            var Q25;
            Q25=makeQuery(id+"F2.imprint","IMPRINT",FACE,{"disambiguationData":[TD([[makeQuery(id+"F2.imprint","IMPRINT",EDGE,{"derivedFrom":sQuery(id+"F2.wireOp",EDGE,"E3.6.0.38")}),-1.0]])]});
            var Q26;
            Q26=makeQuery(id+"F2.imprint","IMPRINT",FACE,{"disambiguationData":[TD([[makeQuery(id+"F2.imprint","IMPRINT",EDGE,{"derivedFrom":sQuery(id+"F2.wireOp",EDGE,"E3.6.0.7")}),-1.0]])]});
            var Q27;
            Q27=makeQuery(id+"F2.imprint","IMPRINT",FACE,{"disambiguationData":[TD([[makeQuery(id+"F2.imprint","IMPRINT",EDGE,{"derivedFrom":sQuery(id+"F2.wireOp",EDGE,"E3.6.0.26")}),-1.0]])]});
            var Q28;
            Q28=makeQuery(id+"F2.imprint","IMPRINT",FACE,{"disambiguationData":[TD([[makeQuery(id+"F2.imprint","IMPRINT",EDGE,{"derivedFrom":sQuery(id+"F2.wireOp",EDGE,"E3.8.0.26")}),-1.0]])]});
            var Q29;
            Q29=makeQuery(id+"F2.imprint","IMPRINT",FACE,{"disambiguationData":[TD([[makeQuery(id+"F2.imprint","IMPRINT",EDGE,{"derivedFrom":sQuery(id+"F2.wireOp",EDGE,"E3.8.0.7")}),-1.0]])]});
            var Q30;
            Q30=makeQuery(id+"F2.imprint","IMPRINT",FACE,{"disambiguationData":[TD([[makeQuery(id+"F2.imprint","IMPRINT",EDGE,{"derivedFrom":sQuery(id+"F2.wireOp",EDGE,"E3.8.0.38")}),-1.0]])]});
            var Q31;
            Q31=makeQuery(id+"F2.imprint","IMPRINT",FACE,{"disambiguationData":[TD([[makeQuery(id+"F2.imprint","IMPRINT",EDGE,{"derivedFrom":sQuery(id+"F2.wireOp",EDGE,"E3.8.0.8")}),-1.0]])]});
            var Q32;
            Q32=makeQuery(id+"F2.imprint","IMPRINT",FACE,{"disambiguationData":[TD([[makeQuery(id+"F2.imprint","IMPRINT",EDGE,{"derivedFrom":sQuery(id+"F2.wireOp",EDGE,"E3.8.0.39")}),-1.0]])]});
            var Q33;
            Q33=makeQuery(id+"F2.imprint","IMPRINT",FACE,{"disambiguationData":[TD([[makeQuery(id+"F2.imprint","IMPRINT",EDGE,{"derivedFrom":sQuery(id+"F2.wireOp",EDGE,"E3.8.0.0")}),-1.0]])]});
            var Q34;
            Q34=makeQuery(id+"F2.imprint","IMPRINT",FACE,{"disambiguationData":[TD([[makeQuery(id+"F2.imprint","IMPRINT",EDGE,{"derivedFrom":sQuery(id+"F2.wireOp",EDGE,"E3.8.0.20")}),1.0]])]});
            var Q35;
            Q35=makeQuery(id+"F2.imprint","IMPRINT",FACE,{"disambiguationData":[TD([[makeQuery(id+"F2.imprint","IMPRINT",EDGE,{"derivedFrom":sQuery(id+"F2.wireOp",EDGE,"E3.10.0.20")}),1.0]])]});
            var Q36;
            Q36=makeQuery(id+"F2.imprint","IMPRINT",FACE,{"disambiguationData":[TD([[makeQuery(id+"F2.imprint","IMPRINT",EDGE,{"derivedFrom":sQuery(id+"F2.wireOp",EDGE,"E3.10.0.0")}),-1.0]])]});
            var Q37;
            Q37=makeQuery(id+"F2.imprint","IMPRINT",FACE,{"disambiguationData":[TD([[makeQuery(id+"F2.imprint","IMPRINT",EDGE,{"derivedFrom":sQuery(id+"F2.wireOp",EDGE,"E3.12.0.0")}),-1.0]])]});
            var Q38;
            Q38=makeQuery(id+"F2.imprint","IMPRINT",FACE,{"disambiguationData":[TD([[makeQuery(id+"F2.imprint","IMPRINT",EDGE,{"derivedFrom":sQuery(id+"F2.wireOp",EDGE,"E3.12.0.20")}),1.0]])]});
            var Q39;
            Q39=makeQuery(id+"F2.imprint","IMPRINT",FACE,{"disambiguationData":[TD([[makeQuery(id+"F2.imprint","IMPRINT",EDGE,{"derivedFrom":sQuery(id+"F2.wireOp",EDGE,"E3.14.0.20")}),1.0]])]});
            var Q40;
            Q40=makeQuery(id+"F2.imprint","IMPRINT",FACE,{"disambiguationData":[TD([[makeQuery(id+"F2.imprint","IMPRINT",EDGE,{"derivedFrom":sQuery(id+"F2.wireOp",EDGE,"E3.14.0.39")}),-1.0]])]});
            var Q41;
            Q41=makeQuery(id+"F2.imprint","IMPRINT",FACE,{"disambiguationData":[TD([[makeQuery(id+"F2.imprint","IMPRINT",EDGE,{"derivedFrom":sQuery(id+"F2.wireOp",EDGE,"E3.12.0.39")}),-1.0]])]});
            var Q42;
            Q42=makeQuery(id+"F2.imprint","IMPRINT",FACE,{"disambiguationData":[TD([[makeQuery(id+"F2.imprint","IMPRINT",EDGE,{"derivedFrom":sQuery(id+"F2.wireOp",EDGE,"E3.10.0.39")}),-1.0]])]});
            var Q43;
            Q43=makeQuery(id+"F2.imprint","IMPRINT",FACE,{"disambiguationData":[TD([[makeQuery(id+"F2.imprint","IMPRINT",EDGE,{"derivedFrom":sQuery(id+"F2.wireOp",EDGE,"E3.10.0.8")}),-1.0]])]});
            var Q44;
            Q44=makeQuery(id+"F2.imprint","IMPRINT",FACE,{"disambiguationData":[TD([[makeQuery(id+"F2.imprint","IMPRINT",EDGE,{"derivedFrom":sQuery(id+"F2.wireOp",EDGE,"E3.12.0.8")}),-1.0]])]});
            var Q45;
            Q45=makeQuery(id+"F2.imprint","IMPRINT",FACE,{"disambiguationData":[TD([[makeQuery(id+"F2.imprint","IMPRINT",EDGE,{"derivedFrom":sQuery(id+"F2.wireOp",EDGE,"E3.14.0.8")}),-1.0]])]});
            var Q46;
            Q46=makeQuery(id+"F2.imprint","IMPRINT",FACE,{"disambiguationData":[TD([[makeQuery(id+"F2.imprint","IMPRINT",EDGE,{"derivedFrom":sQuery(id+"F2.wireOp",EDGE,"E3.14.0.38")}),-1.0]])]});
            var Q47;
            Q47=makeQuery(id+"F2.imprint","IMPRINT",FACE,{"disambiguationData":[TD([[makeQuery(id+"F2.imprint","IMPRINT",EDGE,{"derivedFrom":sQuery(id+"F2.wireOp",EDGE,"E3.14.0.7")}),-1.0]])]});
            var Q48;
            Q48=makeQuery(id+"F2.imprint","IMPRINT",FACE,{"disambiguationData":[TD([[makeQuery(id+"F2.imprint","IMPRINT",EDGE,{"derivedFrom":sQuery(id+"F2.wireOp",EDGE,"E3.12.0.7")}),-1.0]])]});
            var Q49;
            Q49=makeQuery(id+"F2.imprint","IMPRINT",FACE,{"disambiguationData":[TD([[makeQuery(id+"F2.imprint","IMPRINT",EDGE,{"derivedFrom":sQuery(id+"F2.wireOp",EDGE,"E3.12.0.26")}),-1.0]])]});
            var Q50;
            Q50=makeQuery(id+"F2.imprint","IMPRINT",FACE,{"disambiguationData":[TD([[makeQuery(id+"F2.imprint","IMPRINT",EDGE,{"derivedFrom":sQuery(id+"F2.wireOp",EDGE,"E3.10.0.26")}),-1.0]])]});
            var Q51;
            Q51=makeQuery(id+"F2.imprint","IMPRINT",FACE,{"disambiguationData":[TD([[makeQuery(id+"F2.imprint","IMPRINT",EDGE,{"derivedFrom":sQuery(id+"F2.wireOp",EDGE,"E3.10.0.7")}),-1.0]])]});
            var Q52;
            Q52=makeQuery(id+"F2.imprint","IMPRINT",FACE,{"disambiguationData":[TD([[makeQuery(id+"F2.imprint","IMPRINT",EDGE,{"derivedFrom":sQuery(id+"F2.wireOp",EDGE,"E3.10.0.38")}),-1.0]])]});
            var Q53;
            Q53=makeQuery(id+"F2.imprint","IMPRINT",FACE,{"disambiguationData":[TD([[makeQuery(id+"F2.imprint","IMPRINT",EDGE,{"derivedFrom":sQuery(id+"F2.wireOp",EDGE,"E3.12.0.38")}),-1.0]])]});
            var Q54;
            Q54=makeQuery(id+"F2.imprint","IMPRINT",FACE,{"disambiguationData":[TD([[makeQuery(id+"F2.imprint","IMPRINT",EDGE,{"derivedFrom":sQuery(id+"F2.wireOp",EDGE,"E3.14.0.26")}),-1.0]])]});
            var Q55;
            Q55=makeQuery(id+"F2.imprint","IMPRINT",FACE,{"disambiguationData":[TD([[makeQuery(id+"F2.imprint","IMPRINT",EDGE,{"derivedFrom":sQuery(id+"F2.wireOp",EDGE,"E3.16.0.26")}),-1.0]])]});
            var Q56;
            Q56=makeQuery(id+"F2.imprint","IMPRINT",FACE,{"disambiguationData":[TD([[makeQuery(id+"F2.imprint","IMPRINT",EDGE,{"derivedFrom":sQuery(id+"F2.wireOp",EDGE,"E3.16.0.7")}),-1.0]])]});
            var Q57;
            Q57=makeQuery(id+"F2.imprint","IMPRINT",FACE,{"disambiguationData":[TD([[makeQuery(id+"F2.imprint","IMPRINT",EDGE,{"derivedFrom":sQuery(id+"F2.wireOp",EDGE,"E3.16.0.38")}),-1.0]])]});
            var Q58;
            Q58=makeQuery(id+"F2.imprint","IMPRINT",FACE,{"disambiguationData":[TD([[makeQuery(id+"F2.imprint","IMPRINT",EDGE,{"derivedFrom":sQuery(id+"F2.wireOp",EDGE,"E3.16.0.8")}),-1.0]])]});
            var Q59;
            Q59=makeQuery(id+"F2.imprint","IMPRINT",FACE,{"disambiguationData":[TD([[makeQuery(id+"F2.imprint","IMPRINT",EDGE,{"derivedFrom":sQuery(id+"F2.wireOp",EDGE,"E3.16.0.39")}),-1.0]])]});
            var Q60;
            Q60=makeQuery(id+"F2.imprint","IMPRINT",FACE,{"disambiguationData":[TD([[makeQuery(id+"F2.imprint","IMPRINT",EDGE,{"derivedFrom":sQuery(id+"F2.wireOp",EDGE,"E3.16.0.0")}),-1.0]])]});
            var Q61;
            Q61=makeQuery(id+"F2.imprint","IMPRINT",FACE,{"disambiguationData":[TD([[makeQuery(id+"F2.imprint","IMPRINT",EDGE,{"derivedFrom":sQuery(id+"F2.wireOp",EDGE,"E3.18.0.20")}),1.0]])]});
            var Q62;
            Q62=makeQuery(id+"F2.imprint","IMPRINT",FACE,{"disambiguationData":[TD([[makeQuery(id+"F2.imprint","IMPRINT",EDGE,{"derivedFrom":sQuery(id+"F2.wireOp",EDGE,"E3.18.0.0")}),-1.0]])]});
            var Q63;
            Q63=makeQuery(id+"F2.imprint","IMPRINT",FACE,{"disambiguationData":[TD([[makeQuery(id+"F2.imprint","IMPRINT",EDGE,{"derivedFrom":sQuery(id+"F2.wireOp",EDGE,"E3.18.0.39")}),-1.0]])]});
            var Q64;
            Q64=makeQuery(id+"F2.imprint","IMPRINT",FACE,{"disambiguationData":[TD([[makeQuery(id+"F2.imprint","IMPRINT",EDGE,{"derivedFrom":sQuery(id+"F2.wireOp",EDGE,"E3.18.0.8")}),-1.0]])]});
            var Q65;
            Q65=makeQuery(id+"F2.imprint","IMPRINT",FACE,{"disambiguationData":[TD([[makeQuery(id+"F2.imprint","IMPRINT",EDGE,{"derivedFrom":sQuery(id+"F2.wireOp",EDGE,"E3.18.0.38")}),-1.0]])]});
            var Q66;
            Q66=makeQuery(id+"F2.imprint","IMPRINT",FACE,{"disambiguationData":[TD([[makeQuery(id+"F2.imprint","IMPRINT",EDGE,{"derivedFrom":sQuery(id+"F2.wireOp",EDGE,"E3.18.0.7")}),-1.0]])]});
            var Q67;
            Q67=makeQuery(id+"F2.imprint","IMPRINT",FACE,{"disambiguationData":[TD([[makeQuery(id+"F2.imprint","IMPRINT",EDGE,{"derivedFrom":sQuery(id+"F2.wireOp",EDGE,"E3.18.0.26")}),-1.0]])]});
            var Q68;
            Q68=makeQuery(id+"F2.imprint","IMPRINT",FACE,{"disambiguationData":[TD([[makeQuery(id+"F2.imprint","IMPRINT",EDGE,{"derivedFrom":sQuery(id+"F2.wireOp",EDGE,"E3.20.0.26")}),-1.0]])]});
            var Q69;
            Q69=makeQuery(id+"F2.imprint","IMPRINT",FACE,{"disambiguationData":[TD([[makeQuery(id+"F2.imprint","IMPRINT",EDGE,{"derivedFrom":sQuery(id+"F2.wireOp",EDGE,"E3.20.0.5")}),1.0]])]});
            var Q70;
            Q70=makeQuery(id+"F2.imprint","IMPRINT",FACE,{"disambiguationData":[TD([[makeQuery(id+"F2.imprint","IMPRINT",EDGE,{"derivedFrom":sQuery(id+"F2.wireOp",EDGE,"E3.20.0.31")}),1.0]])]});
            var Q71;
            Q71=makeQuery(id+"F2.imprint","IMPRINT",FACE,{"disambiguationData":[TD([[makeQuery(id+"F2.imprint","IMPRINT",EDGE,{"derivedFrom":sQuery(id+"F2.wireOp",EDGE,"E3.20.0.3")}),1.0]])]});
            var Q72;
            Q72=makeQuery(id+"F2.imprint","IMPRINT",FACE,{"disambiguationData":[TD([[makeQuery(id+"F2.imprint","IMPRINT",EDGE,{"derivedFrom":sQuery(id+"F2.wireOp",EDGE,"E3.20.0.32")}),1.0]])]});
            var Q73;
            Q73=makeQuery(id+"F2.imprint","IMPRINT",FACE,{"disambiguationData":[TD([[makeQuery(id+"F2.imprint","IMPRINT",EDGE,{"derivedFrom":sQuery(id+"F2.wireOp",EDGE,"E3.20.0.0")}),-1.0]])]});
            var Q74;
            Q74=makeQuery(id+"F2.imprint","IMPRINT",FACE,{"disambiguationData":[TD([[makeQuery(id+"F2.imprint","IMPRINT",EDGE,{"derivedFrom":sQuery(id+"F2.wireOp",EDGE,"E3.20.0.17")}),1.0]])]});
            var Q75;
            Q75=makeQuery(id+"F2.imprint","IMPRINT",FACE,{"disambiguationData":[TD([[makeQuery(id+"F2.imprint","IMPRINT",EDGE,{"derivedFrom":sQuery(id+"F2.wireOp",EDGE,"E3.14.0.0")}),-1.0]])]});
            var Q76;
            Q76=makeQuery(id+"F2.imprint","IMPRINT",FACE,{"disambiguationData":[TD([[makeQuery(id+"F2.imprint","IMPRINT",EDGE,{"derivedFrom":sQuery(id+"F2.wireOp",EDGE,"E3.16.0.20")}),1.0]])]});
            extrude(context, id + "F3", {"entities" : qUnion([Q0, Q1, Q2, Q3, Q4, Q5, Q6, Q7, Q8, Q9, Q10, Q11, Q12, Q13, Q14, Q15, Q16, Q17, Q18, Q19, Q20, Q21, Q22, Q23, Q24, Q25, Q26, Q27, Q28, Q29, Q30, Q31, Q32, Q33, Q34, Q35, Q36, Q37, Q38, Q39, Q40, Q41, Q42, Q43, Q44, Q45, Q46, Q47, Q48, Q49, Q50, Q51, Q52, Q53, Q54, Q55, Q56, Q57, Q58, Q59, Q60, Q61, Q62, Q63, Q64, Q65, Q66, Q67, Q68, Q69, Q70, Q71, Q72, Q73, Q74, Q75, Q76]), "operationType" : NewBodyOperationType.REMOVE, "oppositeDirection" : true, "depth" : 25.4 * mm, "offsetDistance" : 25.4 * mm});
        }
        {
            var Q0;
            Q0=makeQuery(id+"F1.opExtrude","CAP_FACE",FACE,{"disambiguationData":[OSD([sQuery(id+"F0.wireOp",EDGE,"E0.bottom"),sQuery(id+"F0.wireOp",EDGE,"E0.top"),sQuery(id+"F0.wireOp",EDGE,"E0.left"),sQuery(id+"F0.wireOp",EDGE,"E0.right")])],"isStart":false});
            var sketch = newSketch(context, id + "F4", { "sketchPlane" : qUnion([Q0])});
            skLineSegment(sketch, "E4.bottom", {"start": v(-168.58, 47.54) * mm, "end": v(-162.23, 47.54) * mm});
            skLineSegment(sketch, "E4.top", {"start": v(-168.58, 41.19) * mm, "end": v(-162.23, 41.19) * mm});
            skLineSegment(sketch, "E4.left", {"start": v(-168.58, 47.54) * mm, "end": v(-168.58, 41.19) * mm});
            skLineSegment(sketch, "E4.right", {"start": v(-162.23, 47.54) * mm, "end": v(-162.23, 41.19) * mm});
            skLineSegment(sketch, "E5.bottom", {"start": v(-168.58, -98.51) * mm, "end": v(-162.23, -98.51) * mm});
            skLineSegment(sketch, "E5.top", {"start": v(-168.58, -92.16) * mm, "end": v(-162.23, -92.16) * mm});
            skLineSegment(sketch, "E5.left", {"start": v(-168.58, -98.51) * mm, "end": v(-168.58, -92.16) * mm});
            skLineSegment(sketch, "E5.right", {"start": v(-162.23, -98.51) * mm, "end": v(-162.23, -92.16) * mm});
            skLineSegment(sketch, "E6.bottom", {"start": v(-73.33, -98.51) * mm, "end": v(-79.68, -98.51) * mm});
            skLineSegment(sketch, "E6.top", {"start": v(-73.33, -92.16) * mm, "end": v(-79.68, -92.16) * mm});
            skLineSegment(sketch, "E6.left", {"start": v(-73.33, -98.51) * mm, "end": v(-73.33, -92.16) * mm});
            skLineSegment(sketch, "E6.right", {"start": v(-79.68, -98.51) * mm, "end": v(-79.68, -92.16) * mm});
            skLineSegment(sketch, "E7.bottom", {"start": v(-73.33, 47.54) * mm, "end": v(-79.68, 47.54) * mm});
            skLineSegment(sketch, "E7.top", {"start": v(-73.33, 41.19) * mm, "end": v(-79.68, 41.19) * mm});
            skLineSegment(sketch, "E7.left", {"start": v(-73.33, 47.54) * mm, "end": v(-73.33, 41.19) * mm});
            skLineSegment(sketch, "E7.right", {"start": v(-79.68, 47.54) * mm, "end": v(-79.68, 41.19) * mm});
            skSolve(sketch);
        }
        {
            var Q0;
            Q0=makeQuery(id+"F4.imprint","IMPRINT",FACE,{"disambiguationData":[TD([[makeQuery(id+"F4.imprint","IMPRINT",EDGE,{"derivedFrom":sQuery(id+"F4.wireOp",EDGE,"E7.bottom")}),-1.0]])]});
            var Q1;
            Q1=makeQuery(id+"F4.imprint","IMPRINT",FACE,{"disambiguationData":[TD([[makeQuery(id+"F4.imprint","IMPRINT",EDGE,{"derivedFrom":sQuery(id+"F4.wireOp",EDGE,"E6.bottom")}),1.0]])]});
            var Q2;
            Q2=makeQuery(id+"F4.imprint","IMPRINT",FACE,{"disambiguationData":[TD([[makeQuery(id+"F4.imprint","IMPRINT",EDGE,{"derivedFrom":sQuery(id+"F4.wireOp",EDGE,"E4.bottom")}),-1.0]])]});
            var Q3;
            Q3=makeQuery(id+"F4.imprint","IMPRINT",FACE,{"disambiguationData":[TD([[makeQuery(id+"F4.imprint","IMPRINT",EDGE,{"derivedFrom":sQuery(id+"F4.wireOp",EDGE,"E5.bottom")}),1.0]])]});
            extrude(context, id + "F5", {"entities" : qUnion([Q0, Q1, Q2, Q3]), "operationType" : NewBodyOperationType.ADD, "depth" : -57.15 * mm, "offsetDistance" : 25.4 * mm});
        }
    });
